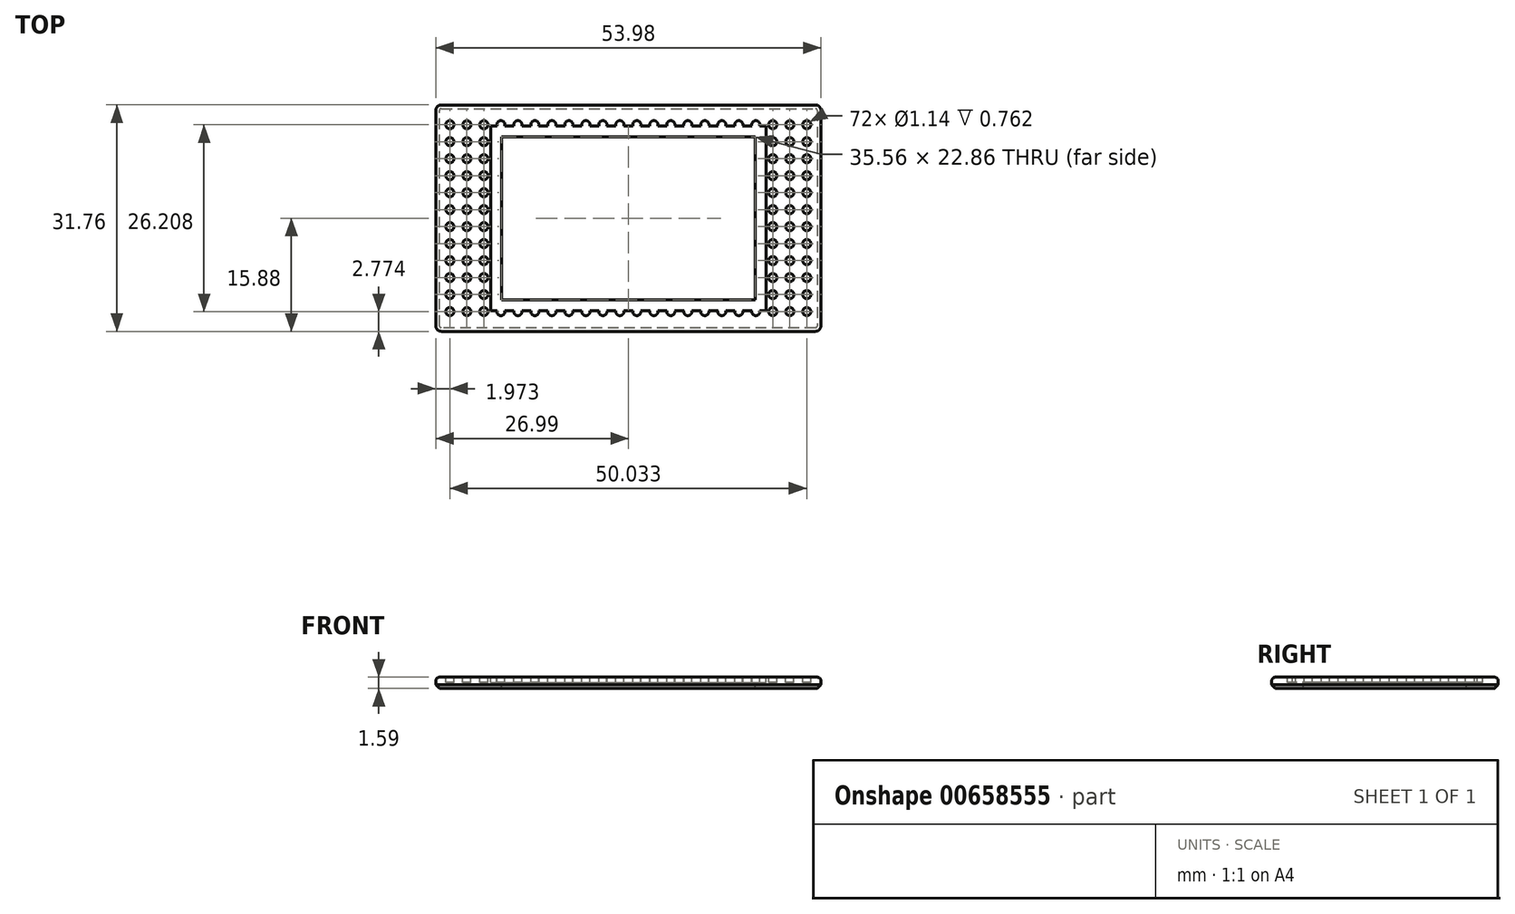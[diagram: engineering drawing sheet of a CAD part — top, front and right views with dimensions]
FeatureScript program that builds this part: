
annotation { "Feature Type Name" : "Feature", "Feature Type Description" : "" }
export const myFeature = defineFeature(function(context is Context, id is Id, definition is map)
    precondition{}
    {
        {
            var Q0;
            Q0=qCreatedBy(makeId("Top.planeOp"),FACE);
            var sketch = newSketch(context, id + "F0", { "sketchPlane" : qUnion([Q0])});
            skLineSegment(sketch, "E0.bottom", {"start": v(-26.99, 15.88) * mm, "end": v(26.99, 15.88) * mm});
            skLineSegment(sketch, "E0.top", {"start": v(-26.99, -15.88) * mm, "end": v(26.99, -15.88) * mm});
            skLineSegment(sketch, "E0.left", {"start": v(-26.99, 15.87) * mm, "end": v(-26.99, -15.88) * mm});
            skLineSegment(sketch, "E0.right", {"start": v(26.99, 15.88) * mm, "end": v(26.99, -15.87) * mm});
            skSolve(sketch);
        }
        {
            var Q0;
            Q0 = qSketchRegion(id + "F0", true);
            extrude(context, id + "F1", {"entities" : qUnion([Q0]), "depth" : 1.59 * mm, "offsetDistance" : 25.4 * mm});
        }
        {
            var Q0;
            Q0=makeQuery(id+"F1.opExtrude","CAP_FACE",FACE,{"disambiguationData":[OSD([sQuery(id+"F0.wireOp",EDGE,"E0.bottom"),sQuery(id+"F0.wireOp",EDGE,"E0.top"),sQuery(id+"F0.wireOp",EDGE,"E0.left"),sQuery(id+"F0.wireOp",EDGE,"E0.right")])],"isStart":false});
            var sketch = newSketch(context, id + "F2", { "sketchPlane" : qUnion([Q0])});
            skCircle(sketch, "E1", {"center": v(-25.02, -13.1) * mm, "radius": 0.57 * mm});
            skCircle(sketch, "E2.0.1.0", {"center": v(-25.02, -10.72) * mm, "radius": 0.57 * mm});
            skCircle(sketch, "E2.0.2.0", {"center": v(-25.02, -8.34) * mm, "radius": 0.57 * mm});
            skCircle(sketch, "E2.0.3.0", {"center": v(-25.02, -5.96) * mm, "radius": 0.57 * mm});
            skCircle(sketch, "E2.0.4.0", {"center": v(-25.02, -3.58) * mm, "radius": 0.57 * mm});
            skCircle(sketch, "E2.0.5.0", {"center": v(-25.02, -1.2) * mm, "radius": 0.57 * mm});
            skCircle(sketch, "E2.0.6.0", {"center": v(-25.02, 1.19) * mm, "radius": 0.57 * mm});
            skCircle(sketch, "E2.0.7.0", {"center": v(-25.02, 3.57) * mm, "radius": 0.57 * mm});
            skCircle(sketch, "E2.0.8.0", {"center": v(-25.02, 5.95) * mm, "radius": 0.57 * mm});
            skCircle(sketch, "E2.0.9.0", {"center": v(-25.02, 8.34) * mm, "radius": 0.57 * mm});
            skCircle(sketch, "E2.0.10.0", {"center": v(-25.02, 10.72) * mm, "radius": 0.57 * mm});
            skCircle(sketch, "E2.0.11.0", {"center": v(-25.02, 13.1) * mm, "radius": 0.57 * mm});
            skCircle(sketch, "E2.1.0.0", {"center": v(-22.63, -13.1) * mm, "radius": 0.57 * mm});
            skCircle(sketch, "E2.1.1.0", {"center": v(-22.63, -10.72) * mm, "radius": 0.57 * mm});
            skCircle(sketch, "E2.1.2.0", {"center": v(-22.63, -8.34) * mm, "radius": 0.57 * mm});
            skCircle(sketch, "E2.1.3.0", {"center": v(-22.63, -5.96) * mm, "radius": 0.57 * mm});
            skCircle(sketch, "E2.1.4.0", {"center": v(-22.63, -3.58) * mm, "radius": 0.57 * mm});
            skCircle(sketch, "E2.1.5.0", {"center": v(-22.63, -1.2) * mm, "radius": 0.57 * mm});
            skCircle(sketch, "E2.1.6.0", {"center": v(-22.63, 1.19) * mm, "radius": 0.57 * mm});
            skCircle(sketch, "E2.1.7.0", {"center": v(-22.63, 3.57) * mm, "radius": 0.57 * mm});
            skCircle(sketch, "E2.1.8.0", {"center": v(-22.63, 5.95) * mm, "radius": 0.57 * mm});
            skCircle(sketch, "E2.1.9.0", {"center": v(-22.63, 8.34) * mm, "radius": 0.57 * mm});
            skCircle(sketch, "E2.1.10.0", {"center": v(-22.63, 10.72) * mm, "radius": 0.57 * mm});
            skCircle(sketch, "E2.1.11.0", {"center": v(-22.63, 13.1) * mm, "radius": 0.57 * mm});
            skCircle(sketch, "E2.2.0.0", {"center": v(-20.25, -13.1) * mm, "radius": 0.57 * mm});
            skCircle(sketch, "E2.2.1.0", {"center": v(-20.25, -10.72) * mm, "radius": 0.57 * mm});
            skCircle(sketch, "E2.2.2.0", {"center": v(-20.25, -8.34) * mm, "radius": 0.57 * mm});
            skCircle(sketch, "E2.2.3.0", {"center": v(-20.25, -5.96) * mm, "radius": 0.57 * mm});
            skCircle(sketch, "E2.2.4.0", {"center": v(-20.25, -3.58) * mm, "radius": 0.57 * mm});
            skCircle(sketch, "E2.2.5.0", {"center": v(-20.25, -1.2) * mm, "radius": 0.57 * mm});
            skCircle(sketch, "E2.2.6.0", {"center": v(-20.25, 1.19) * mm, "radius": 0.57 * mm});
            skCircle(sketch, "E2.2.7.0", {"center": v(-20.25, 3.57) * mm, "radius": 0.57 * mm});
            skCircle(sketch, "E2.2.8.0", {"center": v(-20.25, 5.95) * mm, "radius": 0.57 * mm});
            skCircle(sketch, "E2.2.9.0", {"center": v(-20.25, 8.34) * mm, "radius": 0.57 * mm});
            skCircle(sketch, "E2.2.10.0", {"center": v(-20.25, 10.72) * mm, "radius": 0.57 * mm});
            skCircle(sketch, "E2.2.11.0", {"center": v(-20.25, 13.1) * mm, "radius": 0.57 * mm});
            skCircle(sketch, "E2.3.0.0", {"center": v(-17.87, -13.1) * mm, "radius": 0.57 * mm});
            skCircle(sketch, "E2.3.1.0", {"center": v(-17.87, -10.72) * mm, "radius": 0.57 * mm});
            skCircle(sketch, "E2.3.2.0", {"center": v(-17.87, -8.34) * mm, "radius": 0.57 * mm});
            skCircle(sketch, "E2.3.3.0", {"center": v(-17.87, -5.96) * mm, "radius": 0.57 * mm});
            skCircle(sketch, "E2.3.4.0", {"center": v(-17.87, -3.58) * mm, "radius": 0.57 * mm});
            skCircle(sketch, "E2.3.5.0", {"center": v(-17.87, -1.2) * mm, "radius": 0.57 * mm});
            skCircle(sketch, "E2.3.6.0", {"center": v(-17.87, 1.19) * mm, "radius": 0.57 * mm});
            skCircle(sketch, "E2.3.7.0", {"center": v(-17.87, 3.57) * mm, "radius": 0.57 * mm});
            skCircle(sketch, "E2.3.8.0", {"center": v(-17.87, 5.95) * mm, "radius": 0.57 * mm});
            skCircle(sketch, "E2.3.9.0", {"center": v(-17.87, 8.34) * mm, "radius": 0.57 * mm});
            skCircle(sketch, "E2.3.10.0", {"center": v(-17.87, 10.72) * mm, "radius": 0.57 * mm});
            skCircle(sketch, "E2.3.11.0", {"center": v(-17.87, 13.1) * mm, "radius": 0.57 * mm});
            skCircle(sketch, "E2.4.0.0", {"center": v(-15.49, -13.1) * mm, "radius": 0.57 * mm});
            skCircle(sketch, "E2.4.1.0", {"center": v(-15.49, -10.72) * mm, "radius": 0.57 * mm});
            skCircle(sketch, "E2.4.2.0", {"center": v(-15.49, -8.34) * mm, "radius": 0.57 * mm});
            skCircle(sketch, "E2.4.3.0", {"center": v(-15.49, -5.96) * mm, "radius": 0.57 * mm});
            skCircle(sketch, "E2.4.4.0", {"center": v(-15.49, -3.58) * mm, "radius": 0.57 * mm});
            skCircle(sketch, "E2.4.5.0", {"center": v(-15.49, -1.2) * mm, "radius": 0.57 * mm});
            skCircle(sketch, "E2.4.6.0", {"center": v(-15.49, 1.19) * mm, "radius": 0.57 * mm});
            skCircle(sketch, "E2.4.7.0", {"center": v(-15.49, 3.57) * mm, "radius": 0.57 * mm});
            skCircle(sketch, "E2.4.8.0", {"center": v(-15.49, 5.95) * mm, "radius": 0.57 * mm});
            skCircle(sketch, "E2.4.9.0", {"center": v(-15.49, 8.34) * mm, "radius": 0.57 * mm});
            skCircle(sketch, "E2.4.10.0", {"center": v(-15.49, 10.72) * mm, "radius": 0.57 * mm});
            skCircle(sketch, "E2.4.11.0", {"center": v(-15.49, 13.1) * mm, "radius": 0.57 * mm});
            skCircle(sketch, "E2.5.0.0", {"center": v(-13.1, -13.1) * mm, "radius": 0.57 * mm});
            skCircle(sketch, "E2.5.1.0", {"center": v(-13.1, -10.72) * mm, "radius": 0.57 * mm});
            skCircle(sketch, "E2.5.2.0", {"center": v(-13.1, -8.34) * mm, "radius": 0.57 * mm});
            skCircle(sketch, "E2.5.3.0", {"center": v(-13.1, -5.96) * mm, "radius": 0.57 * mm});
            skCircle(sketch, "E2.5.4.0", {"center": v(-13.1, -3.58) * mm, "radius": 0.57 * mm});
            skCircle(sketch, "E2.5.5.0", {"center": v(-13.1, -1.2) * mm, "radius": 0.57 * mm});
            skCircle(sketch, "E2.5.6.0", {"center": v(-13.1, 1.19) * mm, "radius": 0.57 * mm});
            skCircle(sketch, "E2.5.7.0", {"center": v(-13.1, 3.57) * mm, "radius": 0.57 * mm});
            skCircle(sketch, "E2.5.8.0", {"center": v(-13.1, 5.95) * mm, "radius": 0.57 * mm});
            skCircle(sketch, "E2.5.9.0", {"center": v(-13.1, 8.34) * mm, "radius": 0.57 * mm});
            skCircle(sketch, "E2.5.10.0", {"center": v(-13.1, 10.72) * mm, "radius": 0.57 * mm});
            skCircle(sketch, "E2.5.11.0", {"center": v(-13.1, 13.1) * mm, "radius": 0.57 * mm});
            skCircle(sketch, "E2.6.0.0", {"center": v(-10.72, -13.1) * mm, "radius": 0.57 * mm});
            skCircle(sketch, "E2.6.1.0", {"center": v(-10.72, -10.72) * mm, "radius": 0.57 * mm});
            skCircle(sketch, "E2.6.2.0", {"center": v(-10.72, -8.34) * mm, "radius": 0.57 * mm});
            skCircle(sketch, "E2.6.3.0", {"center": v(-10.72, -5.96) * mm, "radius": 0.57 * mm});
            skCircle(sketch, "E2.6.4.0", {"center": v(-10.72, -3.58) * mm, "radius": 0.57 * mm});
            skCircle(sketch, "E2.6.5.0", {"center": v(-10.72, -1.2) * mm, "radius": 0.57 * mm});
            skCircle(sketch, "E2.6.6.0", {"center": v(-10.72, 1.19) * mm, "radius": 0.57 * mm});
            skCircle(sketch, "E2.6.7.0", {"center": v(-10.72, 3.57) * mm, "radius": 0.57 * mm});
            skCircle(sketch, "E2.6.8.0", {"center": v(-10.72, 5.95) * mm, "radius": 0.57 * mm});
            skCircle(sketch, "E2.6.9.0", {"center": v(-10.72, 8.34) * mm, "radius": 0.57 * mm});
            skCircle(sketch, "E2.6.10.0", {"center": v(-10.72, 10.72) * mm, "radius": 0.57 * mm});
            skCircle(sketch, "E2.6.11.0", {"center": v(-10.72, 13.1) * mm, "radius": 0.57 * mm});
            skCircle(sketch, "E2.7.0.0", {"center": v(-8.34, -13.1) * mm, "radius": 0.57 * mm});
            skCircle(sketch, "E2.7.1.0", {"center": v(-8.34, -10.72) * mm, "radius": 0.57 * mm});
            skCircle(sketch, "E2.7.2.0", {"center": v(-8.34, -8.34) * mm, "radius": 0.57 * mm});
            skCircle(sketch, "E2.7.3.0", {"center": v(-8.34, -5.96) * mm, "radius": 0.57 * mm});
            skCircle(sketch, "E2.7.4.0", {"center": v(-8.34, -3.58) * mm, "radius": 0.57 * mm});
            skCircle(sketch, "E2.7.5.0", {"center": v(-8.34, -1.2) * mm, "radius": 0.57 * mm});
            skCircle(sketch, "E2.7.6.0", {"center": v(-8.34, 1.19) * mm, "radius": 0.57 * mm});
            skCircle(sketch, "E2.7.7.0", {"center": v(-8.34, 3.57) * mm, "radius": 0.57 * mm});
            skCircle(sketch, "E2.7.8.0", {"center": v(-8.34, 5.95) * mm, "radius": 0.57 * mm});
            skCircle(sketch, "E2.7.9.0", {"center": v(-8.34, 8.34) * mm, "radius": 0.57 * mm});
            skCircle(sketch, "E2.7.10.0", {"center": v(-8.34, 10.72) * mm, "radius": 0.57 * mm});
            skCircle(sketch, "E2.7.11.0", {"center": v(-8.34, 13.1) * mm, "radius": 0.57 * mm});
            skCircle(sketch, "E2.8.0.0", {"center": v(-5.96, -13.1) * mm, "radius": 0.57 * mm});
            skCircle(sketch, "E2.8.1.0", {"center": v(-5.96, -10.72) * mm, "radius": 0.57 * mm});
            skCircle(sketch, "E2.8.2.0", {"center": v(-5.96, -8.34) * mm, "radius": 0.57 * mm});
            skCircle(sketch, "E2.8.3.0", {"center": v(-5.96, -5.96) * mm, "radius": 0.57 * mm});
            skCircle(sketch, "E2.8.4.0", {"center": v(-5.96, -3.58) * mm, "radius": 0.57 * mm});
            skCircle(sketch, "E2.8.5.0", {"center": v(-5.96, -1.2) * mm, "radius": 0.57 * mm});
            skCircle(sketch, "E2.8.6.0", {"center": v(-5.96, 1.19) * mm, "radius": 0.57 * mm});
            skCircle(sketch, "E2.8.7.0", {"center": v(-5.96, 3.57) * mm, "radius": 0.57 * mm});
            skCircle(sketch, "E2.8.8.0", {"center": v(-5.96, 5.95) * mm, "radius": 0.57 * mm});
            skCircle(sketch, "E2.8.9.0", {"center": v(-5.96, 8.34) * mm, "radius": 0.57 * mm});
            skCircle(sketch, "E2.8.10.0", {"center": v(-5.96, 10.72) * mm, "radius": 0.57 * mm});
            skCircle(sketch, "E2.8.11.0", {"center": v(-5.96, 13.1) * mm, "radius": 0.57 * mm});
            skCircle(sketch, "E2.9.0.0", {"center": v(-3.57, -13.1) * mm, "radius": 0.57 * mm});
            skCircle(sketch, "E2.9.1.0", {"center": v(-3.57, -10.72) * mm, "radius": 0.57 * mm});
            skCircle(sketch, "E2.9.2.0", {"center": v(-3.57, -8.34) * mm, "radius": 0.57 * mm});
            skCircle(sketch, "E2.9.3.0", {"center": v(-3.57, -5.96) * mm, "radius": 0.57 * mm});
            skCircle(sketch, "E2.9.4.0", {"center": v(-3.57, -3.58) * mm, "radius": 0.57 * mm});
            skCircle(sketch, "E2.9.5.0", {"center": v(-3.57, -1.2) * mm, "radius": 0.57 * mm});
            skCircle(sketch, "E2.9.6.0", {"center": v(-3.57, 1.19) * mm, "radius": 0.57 * mm});
            skCircle(sketch, "E2.9.7.0", {"center": v(-3.57, 3.57) * mm, "radius": 0.57 * mm});
            skCircle(sketch, "E2.9.8.0", {"center": v(-3.57, 5.95) * mm, "radius": 0.57 * mm});
            skCircle(sketch, "E2.9.9.0", {"center": v(-3.57, 8.34) * mm, "radius": 0.57 * mm});
            skCircle(sketch, "E2.9.10.0", {"center": v(-3.57, 10.72) * mm, "radius": 0.57 * mm});
            skCircle(sketch, "E2.9.11.0", {"center": v(-3.57, 13.1) * mm, "radius": 0.57 * mm});
            skCircle(sketch, "E2.10.0.0", {"center": v(-1.2, -13.1) * mm, "radius": 0.57 * mm});
            skCircle(sketch, "E2.10.1.0", {"center": v(-1.2, -10.72) * mm, "radius": 0.57 * mm});
            skCircle(sketch, "E2.10.2.0", {"center": v(-1.2, -8.34) * mm, "radius": 0.57 * mm});
            skCircle(sketch, "E2.10.3.0", {"center": v(-1.2, -5.96) * mm, "radius": 0.57 * mm});
            skCircle(sketch, "E2.10.4.0", {"center": v(-1.2, -3.58) * mm, "radius": 0.57 * mm});
            skCircle(sketch, "E2.10.5.0", {"center": v(-1.2, -1.2) * mm, "radius": 0.57 * mm});
            skCircle(sketch, "E2.10.6.0", {"center": v(-1.2, 1.19) * mm, "radius": 0.57 * mm});
            skCircle(sketch, "E2.10.7.0", {"center": v(-1.2, 3.57) * mm, "radius": 0.57 * mm});
            skCircle(sketch, "E2.10.8.0", {"center": v(-1.2, 5.95) * mm, "radius": 0.57 * mm});
            skCircle(sketch, "E2.10.9.0", {"center": v(-1.2, 8.34) * mm, "radius": 0.57 * mm});
            skCircle(sketch, "E2.10.10.0", {"center": v(-1.2, 10.72) * mm, "radius": 0.57 * mm});
            skCircle(sketch, "E2.10.11.0", {"center": v(-1.2, 13.1) * mm, "radius": 0.57 * mm});
            skCircle(sketch, "E2.11.0.0", {"center": v(1.2, -13.1) * mm, "radius": 0.57 * mm});
            skCircle(sketch, "E2.11.1.0", {"center": v(1.2, -10.72) * mm, "radius": 0.57 * mm});
            skCircle(sketch, "E2.11.2.0", {"center": v(1.2, -8.34) * mm, "radius": 0.57 * mm});
            skCircle(sketch, "E2.11.3.0", {"center": v(1.2, -5.96) * mm, "radius": 0.57 * mm});
            skCircle(sketch, "E2.11.4.0", {"center": v(1.2, -3.58) * mm, "radius": 0.57 * mm});
            skCircle(sketch, "E2.11.5.0", {"center": v(1.2, -1.2) * mm, "radius": 0.57 * mm});
            skCircle(sketch, "E2.11.6.0", {"center": v(1.2, 1.19) * mm, "radius": 0.57 * mm});
            skCircle(sketch, "E2.11.7.0", {"center": v(1.2, 3.57) * mm, "radius": 0.57 * mm});
            skCircle(sketch, "E2.11.8.0", {"center": v(1.2, 5.95) * mm, "radius": 0.57 * mm});
            skCircle(sketch, "E2.11.9.0", {"center": v(1.2, 8.34) * mm, "radius": 0.57 * mm});
            skCircle(sketch, "E2.11.10.0", {"center": v(1.2, 10.72) * mm, "radius": 0.57 * mm});
            skCircle(sketch, "E2.11.11.0", {"center": v(1.2, 13.1) * mm, "radius": 0.57 * mm});
            skCircle(sketch, "E2.12.0.0", {"center": v(3.57, -13.1) * mm, "radius": 0.57 * mm});
            skCircle(sketch, "E2.12.1.0", {"center": v(3.57, -10.72) * mm, "radius": 0.57 * mm});
            skCircle(sketch, "E2.12.2.0", {"center": v(3.57, -8.34) * mm, "radius": 0.57 * mm});
            skCircle(sketch, "E2.12.3.0", {"center": v(3.57, -5.96) * mm, "radius": 0.57 * mm});
            skCircle(sketch, "E2.12.4.0", {"center": v(3.57, -3.58) * mm, "radius": 0.57 * mm});
            skCircle(sketch, "E2.12.5.0", {"center": v(3.57, -1.2) * mm, "radius": 0.57 * mm});
            skCircle(sketch, "E2.12.6.0", {"center": v(3.57, 1.19) * mm, "radius": 0.57 * mm});
            skCircle(sketch, "E2.12.7.0", {"center": v(3.57, 3.57) * mm, "radius": 0.57 * mm});
            skCircle(sketch, "E2.12.8.0", {"center": v(3.57, 5.95) * mm, "radius": 0.57 * mm});
            skCircle(sketch, "E2.12.9.0", {"center": v(3.57, 8.34) * mm, "radius": 0.57 * mm});
            skCircle(sketch, "E2.12.10.0", {"center": v(3.57, 10.72) * mm, "radius": 0.57 * mm});
            skCircle(sketch, "E2.12.11.0", {"center": v(3.57, 13.1) * mm, "radius": 0.57 * mm});
            skCircle(sketch, "E2.13.0.0", {"center": v(5.96, -13.1) * mm, "radius": 0.57 * mm});
            skCircle(sketch, "E2.13.1.0", {"center": v(5.96, -10.72) * mm, "radius": 0.57 * mm});
            skCircle(sketch, "E2.13.2.0", {"center": v(5.96, -8.34) * mm, "radius": 0.57 * mm});
            skCircle(sketch, "E2.13.3.0", {"center": v(5.96, -5.96) * mm, "radius": 0.57 * mm});
            skCircle(sketch, "E2.13.4.0", {"center": v(5.96, -3.58) * mm, "radius": 0.57 * mm});
            skCircle(sketch, "E2.13.5.0", {"center": v(5.96, -1.2) * mm, "radius": 0.57 * mm});
            skCircle(sketch, "E2.13.6.0", {"center": v(5.96, 1.19) * mm, "radius": 0.57 * mm});
            skCircle(sketch, "E2.13.7.0", {"center": v(5.96, 3.57) * mm, "radius": 0.57 * mm});
            skCircle(sketch, "E2.13.8.0", {"center": v(5.96, 5.95) * mm, "radius": 0.57 * mm});
            skCircle(sketch, "E2.13.9.0", {"center": v(5.96, 8.34) * mm, "radius": 0.57 * mm});
            skCircle(sketch, "E2.13.10.0", {"center": v(5.96, 10.72) * mm, "radius": 0.57 * mm});
            skCircle(sketch, "E2.13.11.0", {"center": v(5.96, 13.1) * mm, "radius": 0.57 * mm});
            skCircle(sketch, "E2.14.0.0", {"center": v(8.34, -13.1) * mm, "radius": 0.57 * mm});
            skCircle(sketch, "E2.14.1.0", {"center": v(8.34, -10.72) * mm, "radius": 0.57 * mm});
            skCircle(sketch, "E2.14.2.0", {"center": v(8.34, -8.34) * mm, "radius": 0.57 * mm});
            skCircle(sketch, "E2.14.3.0", {"center": v(8.34, -5.96) * mm, "radius": 0.57 * mm});
            skCircle(sketch, "E2.14.4.0", {"center": v(8.34, -3.58) * mm, "radius": 0.57 * mm});
            skCircle(sketch, "E2.14.5.0", {"center": v(8.34, -1.2) * mm, "radius": 0.57 * mm});
            skCircle(sketch, "E2.14.6.0", {"center": v(8.34, 1.19) * mm, "radius": 0.57 * mm});
            skCircle(sketch, "E2.14.7.0", {"center": v(8.34, 3.57) * mm, "radius": 0.57 * mm});
            skCircle(sketch, "E2.14.8.0", {"center": v(8.34, 5.95) * mm, "radius": 0.57 * mm});
            skCircle(sketch, "E2.14.9.0", {"center": v(8.34, 8.34) * mm, "radius": 0.57 * mm});
            skCircle(sketch, "E2.14.10.0", {"center": v(8.34, 10.72) * mm, "radius": 0.57 * mm});
            skCircle(sketch, "E2.14.11.0", {"center": v(8.34, 13.1) * mm, "radius": 0.57 * mm});
            skCircle(sketch, "E2.15.0.0", {"center": v(10.72, -13.1) * mm, "radius": 0.57 * mm});
            skCircle(sketch, "E2.15.1.0", {"center": v(10.72, -10.72) * mm, "radius": 0.57 * mm});
            skCircle(sketch, "E2.15.2.0", {"center": v(10.72, -8.34) * mm, "radius": 0.57 * mm});
            skCircle(sketch, "E2.15.3.0", {"center": v(10.72, -5.96) * mm, "radius": 0.57 * mm});
            skCircle(sketch, "E2.15.4.0", {"center": v(10.72, -3.58) * mm, "radius": 0.57 * mm});
            skCircle(sketch, "E2.15.5.0", {"center": v(10.72, -1.2) * mm, "radius": 0.57 * mm});
            skCircle(sketch, "E2.15.6.0", {"center": v(10.72, 1.19) * mm, "radius": 0.57 * mm});
            skCircle(sketch, "E2.15.7.0", {"center": v(10.72, 3.57) * mm, "radius": 0.57 * mm});
            skCircle(sketch, "E2.15.8.0", {"center": v(10.72, 5.95) * mm, "radius": 0.57 * mm});
            skCircle(sketch, "E2.15.9.0", {"center": v(10.72, 8.34) * mm, "radius": 0.57 * mm});
            skCircle(sketch, "E2.15.10.0", {"center": v(10.72, 10.72) * mm, "radius": 0.57 * mm});
            skCircle(sketch, "E2.15.11.0", {"center": v(10.72, 13.1) * mm, "radius": 0.57 * mm});
            skCircle(sketch, "E2.16.0.0", {"center": v(13.1, -13.1) * mm, "radius": 0.57 * mm});
            skCircle(sketch, "E2.16.1.0", {"center": v(13.1, -10.72) * mm, "radius": 0.57 * mm});
            skCircle(sketch, "E2.16.2.0", {"center": v(13.1, -8.34) * mm, "radius": 0.57 * mm});
            skCircle(sketch, "E2.16.3.0", {"center": v(13.1, -5.96) * mm, "radius": 0.57 * mm});
            skCircle(sketch, "E2.16.4.0", {"center": v(13.1, -3.58) * mm, "radius": 0.57 * mm});
            skCircle(sketch, "E2.16.5.0", {"center": v(13.1, -1.2) * mm, "radius": 0.57 * mm});
            skCircle(sketch, "E2.16.6.0", {"center": v(13.1, 1.19) * mm, "radius": 0.57 * mm});
            skCircle(sketch, "E2.16.7.0", {"center": v(13.1, 3.57) * mm, "radius": 0.57 * mm});
            skCircle(sketch, "E2.16.8.0", {"center": v(13.1, 5.95) * mm, "radius": 0.57 * mm});
            skCircle(sketch, "E2.16.9.0", {"center": v(13.1, 8.34) * mm, "radius": 0.57 * mm});
            skCircle(sketch, "E2.16.10.0", {"center": v(13.1, 10.72) * mm, "radius": 0.57 * mm});
            skCircle(sketch, "E2.16.11.0", {"center": v(13.1, 13.1) * mm, "radius": 0.57 * mm});
            skCircle(sketch, "E2.17.0.0", {"center": v(15.49, -13.1) * mm, "radius": 0.57 * mm});
            skCircle(sketch, "E2.17.1.0", {"center": v(15.49, -10.72) * mm, "radius": 0.57 * mm});
            skCircle(sketch, "E2.17.2.0", {"center": v(15.49, -8.34) * mm, "radius": 0.57 * mm});
            skCircle(sketch, "E2.17.3.0", {"center": v(15.49, -5.96) * mm, "radius": 0.57 * mm});
            skCircle(sketch, "E2.17.4.0", {"center": v(15.49, -3.58) * mm, "radius": 0.57 * mm});
            skCircle(sketch, "E2.17.5.0", {"center": v(15.49, -1.2) * mm, "radius": 0.57 * mm});
            skCircle(sketch, "E2.17.6.0", {"center": v(15.49, 1.19) * mm, "radius": 0.57 * mm});
            skCircle(sketch, "E2.17.7.0", {"center": v(15.49, 3.57) * mm, "radius": 0.57 * mm});
            skCircle(sketch, "E2.17.8.0", {"center": v(15.49, 5.95) * mm, "radius": 0.57 * mm});
            skCircle(sketch, "E2.17.9.0", {"center": v(15.49, 8.34) * mm, "radius": 0.57 * mm});
            skCircle(sketch, "E2.17.10.0", {"center": v(15.49, 10.72) * mm, "radius": 0.57 * mm});
            skCircle(sketch, "E2.17.11.0", {"center": v(15.49, 13.1) * mm, "radius": 0.57 * mm});
            skCircle(sketch, "E2.18.0.0", {"center": v(17.87, -13.1) * mm, "radius": 0.57 * mm});
            skCircle(sketch, "E2.18.1.0", {"center": v(17.87, -10.72) * mm, "radius": 0.57 * mm});
            skCircle(sketch, "E2.18.2.0", {"center": v(17.87, -8.34) * mm, "radius": 0.57 * mm});
            skCircle(sketch, "E2.18.3.0", {"center": v(17.87, -5.96) * mm, "radius": 0.57 * mm});
            skCircle(sketch, "E2.18.4.0", {"center": v(17.87, -3.58) * mm, "radius": 0.57 * mm});
            skCircle(sketch, "E2.18.5.0", {"center": v(17.87, -1.2) * mm, "radius": 0.57 * mm});
            skCircle(sketch, "E2.18.6.0", {"center": v(17.87, 1.19) * mm, "radius": 0.57 * mm});
            skCircle(sketch, "E2.18.7.0", {"center": v(17.87, 3.57) * mm, "radius": 0.57 * mm});
            skCircle(sketch, "E2.18.8.0", {"center": v(17.87, 5.95) * mm, "radius": 0.57 * mm});
            skCircle(sketch, "E2.18.9.0", {"center": v(17.87, 8.34) * mm, "radius": 0.57 * mm});
            skCircle(sketch, "E2.18.10.0", {"center": v(17.87, 10.72) * mm, "radius": 0.57 * mm});
            skCircle(sketch, "E2.18.11.0", {"center": v(17.87, 13.1) * mm, "radius": 0.57 * mm});
            skCircle(sketch, "E2.19.0.0", {"center": v(20.25, -13.1) * mm, "radius": 0.57 * mm});
            skCircle(sketch, "E2.19.1.0", {"center": v(20.25, -10.72) * mm, "radius": 0.57 * mm});
            skCircle(sketch, "E2.19.2.0", {"center": v(20.25, -8.34) * mm, "radius": 0.57 * mm});
            skCircle(sketch, "E2.19.3.0", {"center": v(20.25, -5.96) * mm, "radius": 0.57 * mm});
            skCircle(sketch, "E2.19.4.0", {"center": v(20.25, -3.58) * mm, "radius": 0.57 * mm});
            skCircle(sketch, "E2.19.5.0", {"center": v(20.25, -1.2) * mm, "radius": 0.57 * mm});
            skCircle(sketch, "E2.19.6.0", {"center": v(20.25, 1.19) * mm, "radius": 0.57 * mm});
            skCircle(sketch, "E2.19.7.0", {"center": v(20.25, 3.57) * mm, "radius": 0.57 * mm});
            skCircle(sketch, "E2.19.8.0", {"center": v(20.25, 5.95) * mm, "radius": 0.57 * mm});
            skCircle(sketch, "E2.19.9.0", {"center": v(20.25, 8.34) * mm, "radius": 0.57 * mm});
            skCircle(sketch, "E2.19.10.0", {"center": v(20.25, 10.72) * mm, "radius": 0.57 * mm});
            skCircle(sketch, "E2.19.11.0", {"center": v(20.25, 13.1) * mm, "radius": 0.57 * mm});
            skCircle(sketch, "E2.20.0.0", {"center": v(22.63, -13.1) * mm, "radius": 0.57 * mm});
            skCircle(sketch, "E2.20.1.0", {"center": v(22.63, -10.72) * mm, "radius": 0.57 * mm});
            skCircle(sketch, "E2.20.2.0", {"center": v(22.63, -8.34) * mm, "radius": 0.57 * mm});
            skCircle(sketch, "E2.20.3.0", {"center": v(22.63, -5.96) * mm, "radius": 0.57 * mm});
            skCircle(sketch, "E2.20.4.0", {"center": v(22.63, -3.58) * mm, "radius": 0.57 * mm});
            skCircle(sketch, "E2.20.5.0", {"center": v(22.63, -1.2) * mm, "radius": 0.57 * mm});
            skCircle(sketch, "E2.20.6.0", {"center": v(22.63, 1.19) * mm, "radius": 0.57 * mm});
            skCircle(sketch, "E2.20.7.0", {"center": v(22.63, 3.57) * mm, "radius": 0.57 * mm});
            skCircle(sketch, "E2.20.8.0", {"center": v(22.63, 5.95) * mm, "radius": 0.57 * mm});
            skCircle(sketch, "E2.20.9.0", {"center": v(22.63, 8.34) * mm, "radius": 0.57 * mm});
            skCircle(sketch, "E2.20.10.0", {"center": v(22.63, 10.72) * mm, "radius": 0.57 * mm});
            skCircle(sketch, "E2.20.11.0", {"center": v(22.63, 13.1) * mm, "radius": 0.57 * mm});
            skCircle(sketch, "E2.21.0.0", {"center": v(25.02, -13.1) * mm, "radius": 0.57 * mm});
            skCircle(sketch, "E2.21.1.0", {"center": v(25.02, -10.72) * mm, "radius": 0.57 * mm});
            skCircle(sketch, "E2.21.2.0", {"center": v(25.02, -8.34) * mm, "radius": 0.57 * mm});
            skCircle(sketch, "E2.21.3.0", {"center": v(25.02, -5.96) * mm, "radius": 0.57 * mm});
            skCircle(sketch, "E2.21.4.0", {"center": v(25.02, -3.58) * mm, "radius": 0.57 * mm});
            skCircle(sketch, "E2.21.5.0", {"center": v(25.02, -1.2) * mm, "radius": 0.57 * mm});
            skCircle(sketch, "E2.21.6.0", {"center": v(25.02, 1.19) * mm, "radius": 0.57 * mm});
            skCircle(sketch, "E2.21.7.0", {"center": v(25.02, 3.57) * mm, "radius": 0.57 * mm});
            skCircle(sketch, "E2.21.8.0", {"center": v(25.02, 5.95) * mm, "radius": 0.57 * mm});
            skCircle(sketch, "E2.21.9.0", {"center": v(25.02, 8.34) * mm, "radius": 0.57 * mm});
            skCircle(sketch, "E2.21.10.0", {"center": v(25.02, 10.72) * mm, "radius": 0.57 * mm});
            skCircle(sketch, "E2.21.11.0", {"center": v(25.02, 13.1) * mm, "radius": 0.57 * mm});
            skLineSegment(sketch, "E2.direction1", {"start": v(-25.02, -13.1) * mm, "end": v(-22.63, -13.1) * mm, "construction": true});
            skLineSegment(sketch, "E2.direction2", {"start": v(-25.02, -13.1) * mm, "end": v(-25.02, -10.72) * mm, "construction": true});
            skSolve(sketch);
        }
        {
            var Q0;
            Q0 = qSketchRegion(id + "F2", true);
            extrude(context, id + "F3", {"entities" : qUnion([Q0]), "operationType" : NewBodyOperationType.REMOVE, "oppositeDirection" : true, "depth" : 0.76 * mm, "offsetDistance" : 25.4 * mm});
        }
        {
            var Q0;
            Q0=makeQuery(id+"F1.opExtrude","SWEPT_EDGE",EDGE,{"disambiguationData":[OSD([sQuery(id+"F0.wireOp",EDGE,"E0.top"),sQuery(id+"F0.wireOp",EDGE,"E0.left")])]});
            var Q1;
            Q1=makeQuery(id+"F1.opExtrude","SWEPT_EDGE",EDGE,{"disambiguationData":[OSD([sQuery(id+"F0.wireOp",EDGE,"E0.bottom"),sQuery(id+"F0.wireOp",EDGE,"E0.left")])]});
            var Q2;
            Q2=makeQuery(id+"F1.opExtrude","SWEPT_EDGE",EDGE,{"disambiguationData":[OSD([sQuery(id+"F0.wireOp",EDGE,"E0.bottom"),sQuery(id+"F0.wireOp",EDGE,"E0.right")])]});
            var Q3;
            Q3=makeQuery(id+"F1.opExtrude","SWEPT_EDGE",EDGE,{"disambiguationData":[OSD([sQuery(id+"F0.wireOp",EDGE,"E0.top"),sQuery(id+"F0.wireOp",EDGE,"E0.right")])]});
            fillet(context, id + "F4", {"entities" : qUnion([Q0, Q1, Q2, Q3]), "radius" : 0.76 * mm, "tangentPropagation" : true, "allowEdgeOverflow" : false});
        }
        {
            var Q0;
            Q0=makeQuery(id+"F1.opExtrude","CAP_EDGE",EDGE,{"disambiguationData":[OSD([sQuery(id+"F0.wireOp",EDGE,"E0.right")])],"isStart":false});
            fillet(context, id + "F5", {"entities" : qUnion([Q0]), "radius" : 0.5 * mm, "tangentPropagation" : true, "allowEdgeOverflow" : false});
        }
        {
            var Q0;
            Q0=makeQuery(id+"F1.opExtrude","CAP_EDGE",EDGE,{"disambiguationData":[OSD([sQuery(id+"F0.wireOp",EDGE,"E0.right")])],"isStart":true});
            chamfer(context, id + "F6", {"entities" : qUnion([Q0]), "width" : 0.5 * mm, "tangentPropagation" : true});
        }
        {
            var Q0;
            Q0=makeQuery(id+"F1.opExtrude","CAP_FACE",FACE,{"disambiguationData":[OSD([sQuery(id+"F0.wireOp",EDGE,"E0.bottom"),sQuery(id+"F0.wireOp",EDGE,"E0.top"),sQuery(id+"F0.wireOp",EDGE,"E0.left"),sQuery(id+"F0.wireOp",EDGE,"E0.right")])],"isStart":false});
            var sketch = newSketch(context, id + "F7", { "sketchPlane" : qUnion([Q0])});
            skLineSegment(sketch, "E3.bottom", {"start": v(-19.3, 12.95) * mm, "end": v(19.3, 12.95) * mm});
            skLineSegment(sketch, "E3.top", {"start": v(-19.3, -12.95) * mm, "end": v(19.3, -12.95) * mm});
            skLineSegment(sketch, "E3.left", {"start": v(-19.3, 12.95) * mm, "end": v(-19.3, -12.95) * mm});
            skLineSegment(sketch, "E3.right", {"start": v(19.3, 12.95) * mm, "end": v(19.3, -12.95) * mm});
            skSolve(sketch);
        }
        {
            var Q0;
            Q0 = qSketchRegion(id + "F7", true);
            extrude(context, id + "F8", {"entities" : qUnion([Q0]), "operationType" : NewBodyOperationType.REMOVE, "oppositeDirection" : true, "depth" : 0.76 * mm, "offsetDistance" : 25.4 * mm});
        }
        {
            var Q0;
            Q0=makeQuery(id+"F8.boolean.opBoolean","MERGE",FACE,{"derivedFrom":[makeQuery(id+"F3.boolean.opBoolean","COPY",FACE,{"derivedFrom":makeQuery(id+"F3.opExtrude","CAP_FACE",FACE,{"disambiguationData":[OSD([sQuery(id+"F2.wireOp",EDGE,"E2.3.0.0")])],"isStart":false})}),makeQuery(id+"F3.boolean.opBoolean","COPY",FACE,{"derivedFrom":makeQuery(id+"F3.opExtrude","CAP_FACE",FACE,{"disambiguationData":[OSD([sQuery(id+"F2.wireOp",EDGE,"E2.3.1.0")])],"isStart":false})}),makeQuery(id+"F3.boolean.opBoolean","COPY",FACE,{"derivedFrom":makeQuery(id+"F3.opExtrude","CAP_FACE",FACE,{"disambiguationData":[OSD([sQuery(id+"F2.wireOp",EDGE,"E2.3.2.0")])],"isStart":false})}),makeQuery(id+"F3.boolean.opBoolean","COPY",FACE,{"derivedFrom":makeQuery(id+"F3.opExtrude","CAP_FACE",FACE,{"disambiguationData":[OSD([sQuery(id+"F2.wireOp",EDGE,"E2.3.3.0")])],"isStart":false})}),makeQuery(id+"F3.boolean.opBoolean","COPY",FACE,{"derivedFrom":makeQuery(id+"F3.opExtrude","CAP_FACE",FACE,{"disambiguationData":[OSD([sQuery(id+"F2.wireOp",EDGE,"E2.3.4.0")])],"isStart":false})}),makeQuery(id+"F3.boolean.opBoolean","COPY",FACE,{"derivedFrom":makeQuery(id+"F3.opExtrude","CAP_FACE",FACE,{"disambiguationData":[OSD([sQuery(id+"F2.wireOp",EDGE,"E2.3.5.0")])],"isStart":false})}),makeQuery(id+"F3.boolean.opBoolean","COPY",FACE,{"derivedFrom":makeQuery(id+"F3.opExtrude","CAP_FACE",FACE,{"disambiguationData":[OSD([sQuery(id+"F2.wireOp",EDGE,"E2.3.6.0")])],"isStart":false})}),makeQuery(id+"F3.boolean.opBoolean","COPY",FACE,{"derivedFrom":makeQuery(id+"F3.opExtrude","CAP_FACE",FACE,{"disambiguationData":[OSD([sQuery(id+"F2.wireOp",EDGE,"E2.3.7.0")])],"isStart":false})}),makeQuery(id+"F3.boolean.opBoolean","COPY",FACE,{"derivedFrom":makeQuery(id+"F3.opExtrude","CAP_FACE",FACE,{"disambiguationData":[OSD([sQuery(id+"F2.wireOp",EDGE,"E2.3.8.0")])],"isStart":false})}),makeQuery(id+"F3.boolean.opBoolean","COPY",FACE,{"derivedFrom":makeQuery(id+"F3.opExtrude","CAP_FACE",FACE,{"disambiguationData":[OSD([sQuery(id+"F2.wireOp",EDGE,"E2.3.9.0")])],"isStart":false})}),makeQuery(id+"F3.boolean.opBoolean","COPY",FACE,{"derivedFrom":makeQuery(id+"F3.opExtrude","CAP_FACE",FACE,{"disambiguationData":[OSD([sQuery(id+"F2.wireOp",EDGE,"E2.3.10.0")])],"isStart":false})}),makeQuery(id+"F3.boolean.opBoolean","COPY",FACE,{"derivedFrom":makeQuery(id+"F3.opExtrude","CAP_FACE",FACE,{"disambiguationData":[OSD([sQuery(id+"F2.wireOp",EDGE,"E2.3.11.0")])],"isStart":false})}),makeQuery(id+"F3.boolean.opBoolean","COPY",FACE,{"derivedFrom":makeQuery(id+"F3.opExtrude","CAP_FACE",FACE,{"disambiguationData":[OSD([sQuery(id+"F2.wireOp",EDGE,"E2.4.0.0")])],"isStart":false})}),makeQuery(id+"F3.boolean.opBoolean","COPY",FACE,{"derivedFrom":makeQuery(id+"F3.opExtrude","CAP_FACE",FACE,{"disambiguationData":[OSD([sQuery(id+"F2.wireOp",EDGE,"E2.4.1.0")])],"isStart":false})}),makeQuery(id+"F3.boolean.opBoolean","COPY",FACE,{"derivedFrom":makeQuery(id+"F3.opExtrude","CAP_FACE",FACE,{"disambiguationData":[OSD([sQuery(id+"F2.wireOp",EDGE,"E2.4.2.0")])],"isStart":false})}),makeQuery(id+"F3.boolean.opBoolean","COPY",FACE,{"derivedFrom":makeQuery(id+"F3.opExtrude","CAP_FACE",FACE,{"disambiguationData":[OSD([sQuery(id+"F2.wireOp",EDGE,"E2.4.3.0")])],"isStart":false})}),makeQuery(id+"F3.boolean.opBoolean","COPY",FACE,{"derivedFrom":makeQuery(id+"F3.opExtrude","CAP_FACE",FACE,{"disambiguationData":[OSD([sQuery(id+"F2.wireOp",EDGE,"E2.4.4.0")])],"isStart":false})}),makeQuery(id+"F3.boolean.opBoolean","COPY",FACE,{"derivedFrom":makeQuery(id+"F3.opExtrude","CAP_FACE",FACE,{"disambiguationData":[OSD([sQuery(id+"F2.wireOp",EDGE,"E2.4.5.0")])],"isStart":false})}),makeQuery(id+"F3.boolean.opBoolean","COPY",FACE,{"derivedFrom":makeQuery(id+"F3.opExtrude","CAP_FACE",FACE,{"disambiguationData":[OSD([sQuery(id+"F2.wireOp",EDGE,"E2.4.6.0")])],"isStart":false})}),makeQuery(id+"F3.boolean.opBoolean","COPY",FACE,{"derivedFrom":makeQuery(id+"F3.opExtrude","CAP_FACE",FACE,{"disambiguationData":[OSD([sQuery(id+"F2.wireOp",EDGE,"E2.4.7.0")])],"isStart":false})}),makeQuery(id+"F3.boolean.opBoolean","COPY",FACE,{"derivedFrom":makeQuery(id+"F3.opExtrude","CAP_FACE",FACE,{"disambiguationData":[OSD([sQuery(id+"F2.wireOp",EDGE,"E2.4.8.0")])],"isStart":false})}),makeQuery(id+"F3.boolean.opBoolean","COPY",FACE,{"derivedFrom":makeQuery(id+"F3.opExtrude","CAP_FACE",FACE,{"disambiguationData":[OSD([sQuery(id+"F2.wireOp",EDGE,"E2.4.9.0")])],"isStart":false})}),makeQuery(id+"F3.boolean.opBoolean","COPY",FACE,{"derivedFrom":makeQuery(id+"F3.opExtrude","CAP_FACE",FACE,{"disambiguationData":[OSD([sQuery(id+"F2.wireOp",EDGE,"E2.4.10.0")])],"isStart":false})}),makeQuery(id+"F3.boolean.opBoolean","COPY",FACE,{"derivedFrom":makeQuery(id+"F3.opExtrude","CAP_FACE",FACE,{"disambiguationData":[OSD([sQuery(id+"F2.wireOp",EDGE,"E2.4.11.0")])],"isStart":false})}),makeQuery(id+"F3.boolean.opBoolean","COPY",FACE,{"derivedFrom":makeQuery(id+"F3.opExtrude","CAP_FACE",FACE,{"disambiguationData":[OSD([sQuery(id+"F2.wireOp",EDGE,"E2.5.0.0")])],"isStart":false})}),makeQuery(id+"F3.boolean.opBoolean","COPY",FACE,{"derivedFrom":makeQuery(id+"F3.opExtrude","CAP_FACE",FACE,{"disambiguationData":[OSD([sQuery(id+"F2.wireOp",EDGE,"E2.5.1.0")])],"isStart":false})}),makeQuery(id+"F3.boolean.opBoolean","COPY",FACE,{"derivedFrom":makeQuery(id+"F3.opExtrude","CAP_FACE",FACE,{"disambiguationData":[OSD([sQuery(id+"F2.wireOp",EDGE,"E2.5.2.0")])],"isStart":false})}),makeQuery(id+"F3.boolean.opBoolean","COPY",FACE,{"derivedFrom":makeQuery(id+"F3.opExtrude","CAP_FACE",FACE,{"disambiguationData":[OSD([sQuery(id+"F2.wireOp",EDGE,"E2.5.3.0")])],"isStart":false})}),makeQuery(id+"F3.boolean.opBoolean","COPY",FACE,{"derivedFrom":makeQuery(id+"F3.opExtrude","CAP_FACE",FACE,{"disambiguationData":[OSD([sQuery(id+"F2.wireOp",EDGE,"E2.5.4.0")])],"isStart":false})}),makeQuery(id+"F3.boolean.opBoolean","COPY",FACE,{"derivedFrom":makeQuery(id+"F3.opExtrude","CAP_FACE",FACE,{"disambiguationData":[OSD([sQuery(id+"F2.wireOp",EDGE,"E2.5.5.0")])],"isStart":false})}),makeQuery(id+"F3.boolean.opBoolean","COPY",FACE,{"derivedFrom":makeQuery(id+"F3.opExtrude","CAP_FACE",FACE,{"disambiguationData":[OSD([sQuery(id+"F2.wireOp",EDGE,"E2.5.6.0")])],"isStart":false})}),makeQuery(id+"F3.boolean.opBoolean","COPY",FACE,{"derivedFrom":makeQuery(id+"F3.opExtrude","CAP_FACE",FACE,{"disambiguationData":[OSD([sQuery(id+"F2.wireOp",EDGE,"E2.5.7.0")])],"isStart":false})}),makeQuery(id+"F3.boolean.opBoolean","COPY",FACE,{"derivedFrom":makeQuery(id+"F3.opExtrude","CAP_FACE",FACE,{"disambiguationData":[OSD([sQuery(id+"F2.wireOp",EDGE,"E2.5.8.0")])],"isStart":false})}),makeQuery(id+"F3.boolean.opBoolean","COPY",FACE,{"derivedFrom":makeQuery(id+"F3.opExtrude","CAP_FACE",FACE,{"disambiguationData":[OSD([sQuery(id+"F2.wireOp",EDGE,"E2.5.9.0")])],"isStart":false})}),makeQuery(id+"F3.boolean.opBoolean","COPY",FACE,{"derivedFrom":makeQuery(id+"F3.opExtrude","CAP_FACE",FACE,{"disambiguationData":[OSD([sQuery(id+"F2.wireOp",EDGE,"E2.5.10.0")])],"isStart":false})}),makeQuery(id+"F3.boolean.opBoolean","COPY",FACE,{"derivedFrom":makeQuery(id+"F3.opExtrude","CAP_FACE",FACE,{"disambiguationData":[OSD([sQuery(id+"F2.wireOp",EDGE,"E2.5.11.0")])],"isStart":false})}),makeQuery(id+"F3.boolean.opBoolean","COPY",FACE,{"derivedFrom":makeQuery(id+"F3.opExtrude","CAP_FACE",FACE,{"disambiguationData":[OSD([sQuery(id+"F2.wireOp",EDGE,"E2.6.0.0")])],"isStart":false})}),makeQuery(id+"F3.boolean.opBoolean","COPY",FACE,{"derivedFrom":makeQuery(id+"F3.opExtrude","CAP_FACE",FACE,{"disambiguationData":[OSD([sQuery(id+"F2.wireOp",EDGE,"E2.6.1.0")])],"isStart":false})}),makeQuery(id+"F3.boolean.opBoolean","COPY",FACE,{"derivedFrom":makeQuery(id+"F3.opExtrude","CAP_FACE",FACE,{"disambiguationData":[OSD([sQuery(id+"F2.wireOp",EDGE,"E2.6.2.0")])],"isStart":false})}),makeQuery(id+"F3.boolean.opBoolean","COPY",FACE,{"derivedFrom":makeQuery(id+"F3.opExtrude","CAP_FACE",FACE,{"disambiguationData":[OSD([sQuery(id+"F2.wireOp",EDGE,"E2.6.3.0")])],"isStart":false})}),makeQuery(id+"F3.boolean.opBoolean","COPY",FACE,{"derivedFrom":makeQuery(id+"F3.opExtrude","CAP_FACE",FACE,{"disambiguationData":[OSD([sQuery(id+"F2.wireOp",EDGE,"E2.6.4.0")])],"isStart":false})}),makeQuery(id+"F3.boolean.opBoolean","COPY",FACE,{"derivedFrom":makeQuery(id+"F3.opExtrude","CAP_FACE",FACE,{"disambiguationData":[OSD([sQuery(id+"F2.wireOp",EDGE,"E2.6.5.0")])],"isStart":false})}),makeQuery(id+"F3.boolean.opBoolean","COPY",FACE,{"derivedFrom":makeQuery(id+"F3.opExtrude","CAP_FACE",FACE,{"disambiguationData":[OSD([sQuery(id+"F2.wireOp",EDGE,"E2.6.6.0")])],"isStart":false})}),makeQuery(id+"F3.boolean.opBoolean","COPY",FACE,{"derivedFrom":makeQuery(id+"F3.opExtrude","CAP_FACE",FACE,{"disambiguationData":[OSD([sQuery(id+"F2.wireOp",EDGE,"E2.6.7.0")])],"isStart":false})}),makeQuery(id+"F3.boolean.opBoolean","COPY",FACE,{"derivedFrom":makeQuery(id+"F3.opExtrude","CAP_FACE",FACE,{"disambiguationData":[OSD([sQuery(id+"F2.wireOp",EDGE,"E2.6.8.0")])],"isStart":false})}),makeQuery(id+"F3.boolean.opBoolean","COPY",FACE,{"derivedFrom":makeQuery(id+"F3.opExtrude","CAP_FACE",FACE,{"disambiguationData":[OSD([sQuery(id+"F2.wireOp",EDGE,"E2.6.9.0")])],"isStart":false})}),makeQuery(id+"F3.boolean.opBoolean","COPY",FACE,{"derivedFrom":makeQuery(id+"F3.opExtrude","CAP_FACE",FACE,{"disambiguationData":[OSD([sQuery(id+"F2.wireOp",EDGE,"E2.6.10.0")])],"isStart":false})}),makeQuery(id+"F3.boolean.opBoolean","COPY",FACE,{"derivedFrom":makeQuery(id+"F3.opExtrude","CAP_FACE",FACE,{"disambiguationData":[OSD([sQuery(id+"F2.wireOp",EDGE,"E2.6.11.0")])],"isStart":false})}),makeQuery(id+"F3.boolean.opBoolean","COPY",FACE,{"derivedFrom":makeQuery(id+"F3.opExtrude","CAP_FACE",FACE,{"disambiguationData":[OSD([sQuery(id+"F2.wireOp",EDGE,"E2.7.0.0")])],"isStart":false})}),makeQuery(id+"F3.boolean.opBoolean","COPY",FACE,{"derivedFrom":makeQuery(id+"F3.opExtrude","CAP_FACE",FACE,{"disambiguationData":[OSD([sQuery(id+"F2.wireOp",EDGE,"E2.7.1.0")])],"isStart":false})}),makeQuery(id+"F3.boolean.opBoolean","COPY",FACE,{"derivedFrom":makeQuery(id+"F3.opExtrude","CAP_FACE",FACE,{"disambiguationData":[OSD([sQuery(id+"F2.wireOp",EDGE,"E2.7.2.0")])],"isStart":false})}),makeQuery(id+"F3.boolean.opBoolean","COPY",FACE,{"derivedFrom":makeQuery(id+"F3.opExtrude","CAP_FACE",FACE,{"disambiguationData":[OSD([sQuery(id+"F2.wireOp",EDGE,"E2.7.3.0")])],"isStart":false})}),makeQuery(id+"F3.boolean.opBoolean","COPY",FACE,{"derivedFrom":makeQuery(id+"F3.opExtrude","CAP_FACE",FACE,{"disambiguationData":[OSD([sQuery(id+"F2.wireOp",EDGE,"E2.7.4.0")])],"isStart":false})}),makeQuery(id+"F3.boolean.opBoolean","COPY",FACE,{"derivedFrom":makeQuery(id+"F3.opExtrude","CAP_FACE",FACE,{"disambiguationData":[OSD([sQuery(id+"F2.wireOp",EDGE,"E2.7.5.0")])],"isStart":false})}),makeQuery(id+"F3.boolean.opBoolean","COPY",FACE,{"derivedFrom":makeQuery(id+"F3.opExtrude","CAP_FACE",FACE,{"disambiguationData":[OSD([sQuery(id+"F2.wireOp",EDGE,"E2.7.6.0")])],"isStart":false})}),makeQuery(id+"F3.boolean.opBoolean","COPY",FACE,{"derivedFrom":makeQuery(id+"F3.opExtrude","CAP_FACE",FACE,{"disambiguationData":[OSD([sQuery(id+"F2.wireOp",EDGE,"E2.7.7.0")])],"isStart":false})}),makeQuery(id+"F3.boolean.opBoolean","COPY",FACE,{"derivedFrom":makeQuery(id+"F3.opExtrude","CAP_FACE",FACE,{"disambiguationData":[OSD([sQuery(id+"F2.wireOp",EDGE,"E2.7.8.0")])],"isStart":false})}),makeQuery(id+"F3.boolean.opBoolean","COPY",FACE,{"derivedFrom":makeQuery(id+"F3.opExtrude","CAP_FACE",FACE,{"disambiguationData":[OSD([sQuery(id+"F2.wireOp",EDGE,"E2.7.9.0")])],"isStart":false})}),makeQuery(id+"F3.boolean.opBoolean","COPY",FACE,{"derivedFrom":makeQuery(id+"F3.opExtrude","CAP_FACE",FACE,{"disambiguationData":[OSD([sQuery(id+"F2.wireOp",EDGE,"E2.7.10.0")])],"isStart":false})}),makeQuery(id+"F3.boolean.opBoolean","COPY",FACE,{"derivedFrom":makeQuery(id+"F3.opExtrude","CAP_FACE",FACE,{"disambiguationData":[OSD([sQuery(id+"F2.wireOp",EDGE,"E2.7.11.0")])],"isStart":false})}),makeQuery(id+"F3.boolean.opBoolean","COPY",FACE,{"derivedFrom":makeQuery(id+"F3.opExtrude","CAP_FACE",FACE,{"disambiguationData":[OSD([sQuery(id+"F2.wireOp",EDGE,"E2.8.0.0")])],"isStart":false})}),makeQuery(id+"F3.boolean.opBoolean","COPY",FACE,{"derivedFrom":makeQuery(id+"F3.opExtrude","CAP_FACE",FACE,{"disambiguationData":[OSD([sQuery(id+"F2.wireOp",EDGE,"E2.8.1.0")])],"isStart":false})}),makeQuery(id+"F3.boolean.opBoolean","COPY",FACE,{"derivedFrom":makeQuery(id+"F3.opExtrude","CAP_FACE",FACE,{"disambiguationData":[OSD([sQuery(id+"F2.wireOp",EDGE,"E2.8.2.0")])],"isStart":false})}),makeQuery(id+"F3.boolean.opBoolean","COPY",FACE,{"derivedFrom":makeQuery(id+"F3.opExtrude","CAP_FACE",FACE,{"disambiguationData":[OSD([sQuery(id+"F2.wireOp",EDGE,"E2.8.3.0")])],"isStart":false})}),makeQuery(id+"F3.boolean.opBoolean","COPY",FACE,{"derivedFrom":makeQuery(id+"F3.opExtrude","CAP_FACE",FACE,{"disambiguationData":[OSD([sQuery(id+"F2.wireOp",EDGE,"E2.8.4.0")])],"isStart":false})}),makeQuery(id+"F3.boolean.opBoolean","COPY",FACE,{"derivedFrom":makeQuery(id+"F3.opExtrude","CAP_FACE",FACE,{"disambiguationData":[OSD([sQuery(id+"F2.wireOp",EDGE,"E2.8.5.0")])],"isStart":false})}),makeQuery(id+"F3.boolean.opBoolean","COPY",FACE,{"derivedFrom":makeQuery(id+"F3.opExtrude","CAP_FACE",FACE,{"disambiguationData":[OSD([sQuery(id+"F2.wireOp",EDGE,"E2.8.6.0")])],"isStart":false})}),makeQuery(id+"F3.boolean.opBoolean","COPY",FACE,{"derivedFrom":makeQuery(id+"F3.opExtrude","CAP_FACE",FACE,{"disambiguationData":[OSD([sQuery(id+"F2.wireOp",EDGE,"E2.8.7.0")])],"isStart":false})}),makeQuery(id+"F3.boolean.opBoolean","COPY",FACE,{"derivedFrom":makeQuery(id+"F3.opExtrude","CAP_FACE",FACE,{"disambiguationData":[OSD([sQuery(id+"F2.wireOp",EDGE,"E2.8.8.0")])],"isStart":false})}),makeQuery(id+"F3.boolean.opBoolean","COPY",FACE,{"derivedFrom":makeQuery(id+"F3.opExtrude","CAP_FACE",FACE,{"disambiguationData":[OSD([sQuery(id+"F2.wireOp",EDGE,"E2.8.9.0")])],"isStart":false})}),makeQuery(id+"F3.boolean.opBoolean","COPY",FACE,{"derivedFrom":makeQuery(id+"F3.opExtrude","CAP_FACE",FACE,{"disambiguationData":[OSD([sQuery(id+"F2.wireOp",EDGE,"E2.8.10.0")])],"isStart":false})}),makeQuery(id+"F3.boolean.opBoolean","COPY",FACE,{"derivedFrom":makeQuery(id+"F3.opExtrude","CAP_FACE",FACE,{"disambiguationData":[OSD([sQuery(id+"F2.wireOp",EDGE,"E2.8.11.0")])],"isStart":false})}),makeQuery(id+"F3.boolean.opBoolean","COPY",FACE,{"derivedFrom":makeQuery(id+"F3.opExtrude","CAP_FACE",FACE,{"disambiguationData":[OSD([sQuery(id+"F2.wireOp",EDGE,"E2.9.0.0")])],"isStart":false})}),makeQuery(id+"F3.boolean.opBoolean","COPY",FACE,{"derivedFrom":makeQuery(id+"F3.opExtrude","CAP_FACE",FACE,{"disambiguationData":[OSD([sQuery(id+"F2.wireOp",EDGE,"E2.9.1.0")])],"isStart":false})}),makeQuery(id+"F3.boolean.opBoolean","COPY",FACE,{"derivedFrom":makeQuery(id+"F3.opExtrude","CAP_FACE",FACE,{"disambiguationData":[OSD([sQuery(id+"F2.wireOp",EDGE,"E2.9.2.0")])],"isStart":false})}),makeQuery(id+"F3.boolean.opBoolean","COPY",FACE,{"derivedFrom":makeQuery(id+"F3.opExtrude","CAP_FACE",FACE,{"disambiguationData":[OSD([sQuery(id+"F2.wireOp",EDGE,"E2.9.3.0")])],"isStart":false})}),makeQuery(id+"F3.boolean.opBoolean","COPY",FACE,{"derivedFrom":makeQuery(id+"F3.opExtrude","CAP_FACE",FACE,{"disambiguationData":[OSD([sQuery(id+"F2.wireOp",EDGE,"E2.9.4.0")])],"isStart":false})}),makeQuery(id+"F3.boolean.opBoolean","COPY",FACE,{"derivedFrom":makeQuery(id+"F3.opExtrude","CAP_FACE",FACE,{"disambiguationData":[OSD([sQuery(id+"F2.wireOp",EDGE,"E2.9.5.0")])],"isStart":false})}),makeQuery(id+"F3.boolean.opBoolean","COPY",FACE,{"derivedFrom":makeQuery(id+"F3.opExtrude","CAP_FACE",FACE,{"disambiguationData":[OSD([sQuery(id+"F2.wireOp",EDGE,"E2.9.6.0")])],"isStart":false})}),makeQuery(id+"F3.boolean.opBoolean","COPY",FACE,{"derivedFrom":makeQuery(id+"F3.opExtrude","CAP_FACE",FACE,{"disambiguationData":[OSD([sQuery(id+"F2.wireOp",EDGE,"E2.9.7.0")])],"isStart":false})}),makeQuery(id+"F3.boolean.opBoolean","COPY",FACE,{"derivedFrom":makeQuery(id+"F3.opExtrude","CAP_FACE",FACE,{"disambiguationData":[OSD([sQuery(id+"F2.wireOp",EDGE,"E2.9.8.0")])],"isStart":false})}),makeQuery(id+"F3.boolean.opBoolean","COPY",FACE,{"derivedFrom":makeQuery(id+"F3.opExtrude","CAP_FACE",FACE,{"disambiguationData":[OSD([sQuery(id+"F2.wireOp",EDGE,"E2.9.9.0")])],"isStart":false})}),makeQuery(id+"F3.boolean.opBoolean","COPY",FACE,{"derivedFrom":makeQuery(id+"F3.opExtrude","CAP_FACE",FACE,{"disambiguationData":[OSD([sQuery(id+"F2.wireOp",EDGE,"E2.9.10.0")])],"isStart":false})}),makeQuery(id+"F3.boolean.opBoolean","COPY",FACE,{"derivedFrom":makeQuery(id+"F3.opExtrude","CAP_FACE",FACE,{"disambiguationData":[OSD([sQuery(id+"F2.wireOp",EDGE,"E2.9.11.0")])],"isStart":false})}),makeQuery(id+"F3.boolean.opBoolean","COPY",FACE,{"derivedFrom":makeQuery(id+"F3.opExtrude","CAP_FACE",FACE,{"disambiguationData":[OSD([sQuery(id+"F2.wireOp",EDGE,"E2.10.0.0")])],"isStart":false})}),makeQuery(id+"F3.boolean.opBoolean","COPY",FACE,{"derivedFrom":makeQuery(id+"F3.opExtrude","CAP_FACE",FACE,{"disambiguationData":[OSD([sQuery(id+"F2.wireOp",EDGE,"E2.10.1.0")])],"isStart":false})}),makeQuery(id+"F3.boolean.opBoolean","COPY",FACE,{"derivedFrom":makeQuery(id+"F3.opExtrude","CAP_FACE",FACE,{"disambiguationData":[OSD([sQuery(id+"F2.wireOp",EDGE,"E2.10.2.0")])],"isStart":false})}),makeQuery(id+"F3.boolean.opBoolean","COPY",FACE,{"derivedFrom":makeQuery(id+"F3.opExtrude","CAP_FACE",FACE,{"disambiguationData":[OSD([sQuery(id+"F2.wireOp",EDGE,"E2.10.3.0")])],"isStart":false})}),makeQuery(id+"F3.boolean.opBoolean","COPY",FACE,{"derivedFrom":makeQuery(id+"F3.opExtrude","CAP_FACE",FACE,{"disambiguationData":[OSD([sQuery(id+"F2.wireOp",EDGE,"E2.10.4.0")])],"isStart":false})}),makeQuery(id+"F3.boolean.opBoolean","COPY",FACE,{"derivedFrom":makeQuery(id+"F3.opExtrude","CAP_FACE",FACE,{"disambiguationData":[OSD([sQuery(id+"F2.wireOp",EDGE,"E2.10.5.0")])],"isStart":false})}),makeQuery(id+"F3.boolean.opBoolean","COPY",FACE,{"derivedFrom":makeQuery(id+"F3.opExtrude","CAP_FACE",FACE,{"disambiguationData":[OSD([sQuery(id+"F2.wireOp",EDGE,"E2.10.6.0")])],"isStart":false})}),makeQuery(id+"F3.boolean.opBoolean","COPY",FACE,{"derivedFrom":makeQuery(id+"F3.opExtrude","CAP_FACE",FACE,{"disambiguationData":[OSD([sQuery(id+"F2.wireOp",EDGE,"E2.10.7.0")])],"isStart":false})}),makeQuery(id+"F3.boolean.opBoolean","COPY",FACE,{"derivedFrom":makeQuery(id+"F3.opExtrude","CAP_FACE",FACE,{"disambiguationData":[OSD([sQuery(id+"F2.wireOp",EDGE,"E2.10.8.0")])],"isStart":false})}),makeQuery(id+"F3.boolean.opBoolean","COPY",FACE,{"derivedFrom":makeQuery(id+"F3.opExtrude","CAP_FACE",FACE,{"disambiguationData":[OSD([sQuery(id+"F2.wireOp",EDGE,"E2.10.9.0")])],"isStart":false})}),makeQuery(id+"F3.boolean.opBoolean","COPY",FACE,{"derivedFrom":makeQuery(id+"F3.opExtrude","CAP_FACE",FACE,{"disambiguationData":[OSD([sQuery(id+"F2.wireOp",EDGE,"E2.10.10.0")])],"isStart":false})}),makeQuery(id+"F3.boolean.opBoolean","COPY",FACE,{"derivedFrom":makeQuery(id+"F3.opExtrude","CAP_FACE",FACE,{"disambiguationData":[OSD([sQuery(id+"F2.wireOp",EDGE,"E2.10.11.0")])],"isStart":false})}),makeQuery(id+"F3.boolean.opBoolean","COPY",FACE,{"derivedFrom":makeQuery(id+"F3.opExtrude","CAP_FACE",FACE,{"disambiguationData":[OSD([sQuery(id+"F2.wireOp",EDGE,"E2.11.0.0")])],"isStart":false})}),makeQuery(id+"F3.boolean.opBoolean","COPY",FACE,{"derivedFrom":makeQuery(id+"F3.opExtrude","CAP_FACE",FACE,{"disambiguationData":[OSD([sQuery(id+"F2.wireOp",EDGE,"E2.11.1.0")])],"isStart":false})}),makeQuery(id+"F3.boolean.opBoolean","COPY",FACE,{"derivedFrom":makeQuery(id+"F3.opExtrude","CAP_FACE",FACE,{"disambiguationData":[OSD([sQuery(id+"F2.wireOp",EDGE,"E2.11.2.0")])],"isStart":false})}),makeQuery(id+"F3.boolean.opBoolean","COPY",FACE,{"derivedFrom":makeQuery(id+"F3.opExtrude","CAP_FACE",FACE,{"disambiguationData":[OSD([sQuery(id+"F2.wireOp",EDGE,"E2.11.3.0")])],"isStart":false})}),makeQuery(id+"F3.boolean.opBoolean","COPY",FACE,{"derivedFrom":makeQuery(id+"F3.opExtrude","CAP_FACE",FACE,{"disambiguationData":[OSD([sQuery(id+"F2.wireOp",EDGE,"E2.11.4.0")])],"isStart":false})}),makeQuery(id+"F3.boolean.opBoolean","COPY",FACE,{"derivedFrom":makeQuery(id+"F3.opExtrude","CAP_FACE",FACE,{"disambiguationData":[OSD([sQuery(id+"F2.wireOp",EDGE,"E2.11.5.0")])],"isStart":false})}),makeQuery(id+"F3.boolean.opBoolean","COPY",FACE,{"derivedFrom":makeQuery(id+"F3.opExtrude","CAP_FACE",FACE,{"disambiguationData":[OSD([sQuery(id+"F2.wireOp",EDGE,"E2.11.6.0")])],"isStart":false})}),makeQuery(id+"F3.boolean.opBoolean","COPY",FACE,{"derivedFrom":makeQuery(id+"F3.opExtrude","CAP_FACE",FACE,{"disambiguationData":[OSD([sQuery(id+"F2.wireOp",EDGE,"E2.11.7.0")])],"isStart":false})}),makeQuery(id+"F3.boolean.opBoolean","COPY",FACE,{"derivedFrom":makeQuery(id+"F3.opExtrude","CAP_FACE",FACE,{"disambiguationData":[OSD([sQuery(id+"F2.wireOp",EDGE,"E2.11.8.0")])],"isStart":false})}),makeQuery(id+"F3.boolean.opBoolean","COPY",FACE,{"derivedFrom":makeQuery(id+"F3.opExtrude","CAP_FACE",FACE,{"disambiguationData":[OSD([sQuery(id+"F2.wireOp",EDGE,"E2.11.9.0")])],"isStart":false})}),makeQuery(id+"F3.boolean.opBoolean","COPY",FACE,{"derivedFrom":makeQuery(id+"F3.opExtrude","CAP_FACE",FACE,{"disambiguationData":[OSD([sQuery(id+"F2.wireOp",EDGE,"E2.11.10.0")])],"isStart":false})}),makeQuery(id+"F3.boolean.opBoolean","COPY",FACE,{"derivedFrom":makeQuery(id+"F3.opExtrude","CAP_FACE",FACE,{"disambiguationData":[OSD([sQuery(id+"F2.wireOp",EDGE,"E2.11.11.0")])],"isStart":false})}),makeQuery(id+"F3.boolean.opBoolean","COPY",FACE,{"derivedFrom":makeQuery(id+"F3.opExtrude","CAP_FACE",FACE,{"disambiguationData":[OSD([sQuery(id+"F2.wireOp",EDGE,"E2.12.0.0")])],"isStart":false})}),makeQuery(id+"F3.boolean.opBoolean","COPY",FACE,{"derivedFrom":makeQuery(id+"F3.opExtrude","CAP_FACE",FACE,{"disambiguationData":[OSD([sQuery(id+"F2.wireOp",EDGE,"E2.12.1.0")])],"isStart":false})}),makeQuery(id+"F3.boolean.opBoolean","COPY",FACE,{"derivedFrom":makeQuery(id+"F3.opExtrude","CAP_FACE",FACE,{"disambiguationData":[OSD([sQuery(id+"F2.wireOp",EDGE,"E2.12.2.0")])],"isStart":false})}),makeQuery(id+"F3.boolean.opBoolean","COPY",FACE,{"derivedFrom":makeQuery(id+"F3.opExtrude","CAP_FACE",FACE,{"disambiguationData":[OSD([sQuery(id+"F2.wireOp",EDGE,"E2.12.3.0")])],"isStart":false})}),makeQuery(id+"F3.boolean.opBoolean","COPY",FACE,{"derivedFrom":makeQuery(id+"F3.opExtrude","CAP_FACE",FACE,{"disambiguationData":[OSD([sQuery(id+"F2.wireOp",EDGE,"E2.12.4.0")])],"isStart":false})}),makeQuery(id+"F3.boolean.opBoolean","COPY",FACE,{"derivedFrom":makeQuery(id+"F3.opExtrude","CAP_FACE",FACE,{"disambiguationData":[OSD([sQuery(id+"F2.wireOp",EDGE,"E2.12.5.0")])],"isStart":false})}),makeQuery(id+"F3.boolean.opBoolean","COPY",FACE,{"derivedFrom":makeQuery(id+"F3.opExtrude","CAP_FACE",FACE,{"disambiguationData":[OSD([sQuery(id+"F2.wireOp",EDGE,"E2.12.6.0")])],"isStart":false})}),makeQuery(id+"F3.boolean.opBoolean","COPY",FACE,{"derivedFrom":makeQuery(id+"F3.opExtrude","CAP_FACE",FACE,{"disambiguationData":[OSD([sQuery(id+"F2.wireOp",EDGE,"E2.12.7.0")])],"isStart":false})}),makeQuery(id+"F3.boolean.opBoolean","COPY",FACE,{"derivedFrom":makeQuery(id+"F3.opExtrude","CAP_FACE",FACE,{"disambiguationData":[OSD([sQuery(id+"F2.wireOp",EDGE,"E2.12.8.0")])],"isStart":false})}),makeQuery(id+"F3.boolean.opBoolean","COPY",FACE,{"derivedFrom":makeQuery(id+"F3.opExtrude","CAP_FACE",FACE,{"disambiguationData":[OSD([sQuery(id+"F2.wireOp",EDGE,"E2.12.9.0")])],"isStart":false})}),makeQuery(id+"F3.boolean.opBoolean","COPY",FACE,{"derivedFrom":makeQuery(id+"F3.opExtrude","CAP_FACE",FACE,{"disambiguationData":[OSD([sQuery(id+"F2.wireOp",EDGE,"E2.12.10.0")])],"isStart":false})}),makeQuery(id+"F3.boolean.opBoolean","COPY",FACE,{"derivedFrom":makeQuery(id+"F3.opExtrude","CAP_FACE",FACE,{"disambiguationData":[OSD([sQuery(id+"F2.wireOp",EDGE,"E2.12.11.0")])],"isStart":false})}),makeQuery(id+"F3.boolean.opBoolean","COPY",FACE,{"derivedFrom":makeQuery(id+"F3.opExtrude","CAP_FACE",FACE,{"disambiguationData":[OSD([sQuery(id+"F2.wireOp",EDGE,"E2.13.0.0")])],"isStart":false})}),makeQuery(id+"F3.boolean.opBoolean","COPY",FACE,{"derivedFrom":makeQuery(id+"F3.opExtrude","CAP_FACE",FACE,{"disambiguationData":[OSD([sQuery(id+"F2.wireOp",EDGE,"E2.13.1.0")])],"isStart":false})}),makeQuery(id+"F3.boolean.opBoolean","COPY",FACE,{"derivedFrom":makeQuery(id+"F3.opExtrude","CAP_FACE",FACE,{"disambiguationData":[OSD([sQuery(id+"F2.wireOp",EDGE,"E2.13.2.0")])],"isStart":false})}),makeQuery(id+"F3.boolean.opBoolean","COPY",FACE,{"derivedFrom":makeQuery(id+"F3.opExtrude","CAP_FACE",FACE,{"disambiguationData":[OSD([sQuery(id+"F2.wireOp",EDGE,"E2.13.3.0")])],"isStart":false})}),makeQuery(id+"F3.boolean.opBoolean","COPY",FACE,{"derivedFrom":makeQuery(id+"F3.opExtrude","CAP_FACE",FACE,{"disambiguationData":[OSD([sQuery(id+"F2.wireOp",EDGE,"E2.13.4.0")])],"isStart":false})}),makeQuery(id+"F3.boolean.opBoolean","COPY",FACE,{"derivedFrom":makeQuery(id+"F3.opExtrude","CAP_FACE",FACE,{"disambiguationData":[OSD([sQuery(id+"F2.wireOp",EDGE,"E2.13.5.0")])],"isStart":false})}),makeQuery(id+"F3.boolean.opBoolean","COPY",FACE,{"derivedFrom":makeQuery(id+"F3.opExtrude","CAP_FACE",FACE,{"disambiguationData":[OSD([sQuery(id+"F2.wireOp",EDGE,"E2.13.6.0")])],"isStart":false})}),makeQuery(id+"F3.boolean.opBoolean","COPY",FACE,{"derivedFrom":makeQuery(id+"F3.opExtrude","CAP_FACE",FACE,{"disambiguationData":[OSD([sQuery(id+"F2.wireOp",EDGE,"E2.13.7.0")])],"isStart":false})}),makeQuery(id+"F3.boolean.opBoolean","COPY",FACE,{"derivedFrom":makeQuery(id+"F3.opExtrude","CAP_FACE",FACE,{"disambiguationData":[OSD([sQuery(id+"F2.wireOp",EDGE,"E2.13.8.0")])],"isStart":false})}),makeQuery(id+"F3.boolean.opBoolean","COPY",FACE,{"derivedFrom":makeQuery(id+"F3.opExtrude","CAP_FACE",FACE,{"disambiguationData":[OSD([sQuery(id+"F2.wireOp",EDGE,"E2.13.9.0")])],"isStart":false})}),makeQuery(id+"F3.boolean.opBoolean","COPY",FACE,{"derivedFrom":makeQuery(id+"F3.opExtrude","CAP_FACE",FACE,{"disambiguationData":[OSD([sQuery(id+"F2.wireOp",EDGE,"E2.13.10.0")])],"isStart":false})}),makeQuery(id+"F3.boolean.opBoolean","COPY",FACE,{"derivedFrom":makeQuery(id+"F3.opExtrude","CAP_FACE",FACE,{"disambiguationData":[OSD([sQuery(id+"F2.wireOp",EDGE,"E2.13.11.0")])],"isStart":false})}),makeQuery(id+"F3.boolean.opBoolean","COPY",FACE,{"derivedFrom":makeQuery(id+"F3.opExtrude","CAP_FACE",FACE,{"disambiguationData":[OSD([sQuery(id+"F2.wireOp",EDGE,"E2.14.0.0")])],"isStart":false})}),makeQuery(id+"F3.boolean.opBoolean","COPY",FACE,{"derivedFrom":makeQuery(id+"F3.opExtrude","CAP_FACE",FACE,{"disambiguationData":[OSD([sQuery(id+"F2.wireOp",EDGE,"E2.14.1.0")])],"isStart":false})}),makeQuery(id+"F3.boolean.opBoolean","COPY",FACE,{"derivedFrom":makeQuery(id+"F3.opExtrude","CAP_FACE",FACE,{"disambiguationData":[OSD([sQuery(id+"F2.wireOp",EDGE,"E2.14.2.0")])],"isStart":false})}),makeQuery(id+"F3.boolean.opBoolean","COPY",FACE,{"derivedFrom":makeQuery(id+"F3.opExtrude","CAP_FACE",FACE,{"disambiguationData":[OSD([sQuery(id+"F2.wireOp",EDGE,"E2.14.3.0")])],"isStart":false})}),makeQuery(id+"F3.boolean.opBoolean","COPY",FACE,{"derivedFrom":makeQuery(id+"F3.opExtrude","CAP_FACE",FACE,{"disambiguationData":[OSD([sQuery(id+"F2.wireOp",EDGE,"E2.14.4.0")])],"isStart":false})}),makeQuery(id+"F3.boolean.opBoolean","COPY",FACE,{"derivedFrom":makeQuery(id+"F3.opExtrude","CAP_FACE",FACE,{"disambiguationData":[OSD([sQuery(id+"F2.wireOp",EDGE,"E2.14.5.0")])],"isStart":false})}),makeQuery(id+"F3.boolean.opBoolean","COPY",FACE,{"derivedFrom":makeQuery(id+"F3.opExtrude","CAP_FACE",FACE,{"disambiguationData":[OSD([sQuery(id+"F2.wireOp",EDGE,"E2.14.6.0")])],"isStart":false})}),makeQuery(id+"F3.boolean.opBoolean","COPY",FACE,{"derivedFrom":makeQuery(id+"F3.opExtrude","CAP_FACE",FACE,{"disambiguationData":[OSD([sQuery(id+"F2.wireOp",EDGE,"E2.14.7.0")])],"isStart":false})}),makeQuery(id+"F3.boolean.opBoolean","COPY",FACE,{"derivedFrom":makeQuery(id+"F3.opExtrude","CAP_FACE",FACE,{"disambiguationData":[OSD([sQuery(id+"F2.wireOp",EDGE,"E2.14.8.0")])],"isStart":false})}),makeQuery(id+"F3.boolean.opBoolean","COPY",FACE,{"derivedFrom":makeQuery(id+"F3.opExtrude","CAP_FACE",FACE,{"disambiguationData":[OSD([sQuery(id+"F2.wireOp",EDGE,"E2.14.9.0")])],"isStart":false})}),makeQuery(id+"F3.boolean.opBoolean","COPY",FACE,{"derivedFrom":makeQuery(id+"F3.opExtrude","CAP_FACE",FACE,{"disambiguationData":[OSD([sQuery(id+"F2.wireOp",EDGE,"E2.14.10.0")])],"isStart":false})}),makeQuery(id+"F3.boolean.opBoolean","COPY",FACE,{"derivedFrom":makeQuery(id+"F3.opExtrude","CAP_FACE",FACE,{"disambiguationData":[OSD([sQuery(id+"F2.wireOp",EDGE,"E2.14.11.0")])],"isStart":false})}),makeQuery(id+"F3.boolean.opBoolean","COPY",FACE,{"derivedFrom":makeQuery(id+"F3.opExtrude","CAP_FACE",FACE,{"disambiguationData":[OSD([sQuery(id+"F2.wireOp",EDGE,"E2.15.0.0")])],"isStart":false})}),makeQuery(id+"F3.boolean.opBoolean","COPY",FACE,{"derivedFrom":makeQuery(id+"F3.opExtrude","CAP_FACE",FACE,{"disambiguationData":[OSD([sQuery(id+"F2.wireOp",EDGE,"E2.15.1.0")])],"isStart":false})}),makeQuery(id+"F3.boolean.opBoolean","COPY",FACE,{"derivedFrom":makeQuery(id+"F3.opExtrude","CAP_FACE",FACE,{"disambiguationData":[OSD([sQuery(id+"F2.wireOp",EDGE,"E2.15.2.0")])],"isStart":false})}),makeQuery(id+"F3.boolean.opBoolean","COPY",FACE,{"derivedFrom":makeQuery(id+"F3.opExtrude","CAP_FACE",FACE,{"disambiguationData":[OSD([sQuery(id+"F2.wireOp",EDGE,"E2.15.3.0")])],"isStart":false})}),makeQuery(id+"F3.boolean.opBoolean","COPY",FACE,{"derivedFrom":makeQuery(id+"F3.opExtrude","CAP_FACE",FACE,{"disambiguationData":[OSD([sQuery(id+"F2.wireOp",EDGE,"E2.15.4.0")])],"isStart":false})}),makeQuery(id+"F3.boolean.opBoolean","COPY",FACE,{"derivedFrom":makeQuery(id+"F3.opExtrude","CAP_FACE",FACE,{"disambiguationData":[OSD([sQuery(id+"F2.wireOp",EDGE,"E2.15.5.0")])],"isStart":false})}),makeQuery(id+"F3.boolean.opBoolean","COPY",FACE,{"derivedFrom":makeQuery(id+"F3.opExtrude","CAP_FACE",FACE,{"disambiguationData":[OSD([sQuery(id+"F2.wireOp",EDGE,"E2.15.6.0")])],"isStart":false})}),makeQuery(id+"F3.boolean.opBoolean","COPY",FACE,{"derivedFrom":makeQuery(id+"F3.opExtrude","CAP_FACE",FACE,{"disambiguationData":[OSD([sQuery(id+"F2.wireOp",EDGE,"E2.15.7.0")])],"isStart":false})}),makeQuery(id+"F3.boolean.opBoolean","COPY",FACE,{"derivedFrom":makeQuery(id+"F3.opExtrude","CAP_FACE",FACE,{"disambiguationData":[OSD([sQuery(id+"F2.wireOp",EDGE,"E2.15.8.0")])],"isStart":false})}),makeQuery(id+"F3.boolean.opBoolean","COPY",FACE,{"derivedFrom":makeQuery(id+"F3.opExtrude","CAP_FACE",FACE,{"disambiguationData":[OSD([sQuery(id+"F2.wireOp",EDGE,"E2.15.9.0")])],"isStart":false})}),makeQuery(id+"F3.boolean.opBoolean","COPY",FACE,{"derivedFrom":makeQuery(id+"F3.opExtrude","CAP_FACE",FACE,{"disambiguationData":[OSD([sQuery(id+"F2.wireOp",EDGE,"E2.15.10.0")])],"isStart":false})}),makeQuery(id+"F3.boolean.opBoolean","COPY",FACE,{"derivedFrom":makeQuery(id+"F3.opExtrude","CAP_FACE",FACE,{"disambiguationData":[OSD([sQuery(id+"F2.wireOp",EDGE,"E2.15.11.0")])],"isStart":false})}),makeQuery(id+"F3.boolean.opBoolean","COPY",FACE,{"derivedFrom":makeQuery(id+"F3.opExtrude","CAP_FACE",FACE,{"disambiguationData":[OSD([sQuery(id+"F2.wireOp",EDGE,"E2.16.0.0")])],"isStart":false})}),makeQuery(id+"F3.boolean.opBoolean","COPY",FACE,{"derivedFrom":makeQuery(id+"F3.opExtrude","CAP_FACE",FACE,{"disambiguationData":[OSD([sQuery(id+"F2.wireOp",EDGE,"E2.16.1.0")])],"isStart":false})}),makeQuery(id+"F3.boolean.opBoolean","COPY",FACE,{"derivedFrom":makeQuery(id+"F3.opExtrude","CAP_FACE",FACE,{"disambiguationData":[OSD([sQuery(id+"F2.wireOp",EDGE,"E2.16.2.0")])],"isStart":false})}),makeQuery(id+"F3.boolean.opBoolean","COPY",FACE,{"derivedFrom":makeQuery(id+"F3.opExtrude","CAP_FACE",FACE,{"disambiguationData":[OSD([sQuery(id+"F2.wireOp",EDGE,"E2.16.3.0")])],"isStart":false})}),makeQuery(id+"F3.boolean.opBoolean","COPY",FACE,{"derivedFrom":makeQuery(id+"F3.opExtrude","CAP_FACE",FACE,{"disambiguationData":[OSD([sQuery(id+"F2.wireOp",EDGE,"E2.16.4.0")])],"isStart":false})}),makeQuery(id+"F3.boolean.opBoolean","COPY",FACE,{"derivedFrom":makeQuery(id+"F3.opExtrude","CAP_FACE",FACE,{"disambiguationData":[OSD([sQuery(id+"F2.wireOp",EDGE,"E2.16.5.0")])],"isStart":false})}),makeQuery(id+"F3.boolean.opBoolean","COPY",FACE,{"derivedFrom":makeQuery(id+"F3.opExtrude","CAP_FACE",FACE,{"disambiguationData":[OSD([sQuery(id+"F2.wireOp",EDGE,"E2.16.6.0")])],"isStart":false})}),makeQuery(id+"F3.boolean.opBoolean","COPY",FACE,{"derivedFrom":makeQuery(id+"F3.opExtrude","CAP_FACE",FACE,{"disambiguationData":[OSD([sQuery(id+"F2.wireOp",EDGE,"E2.16.7.0")])],"isStart":false})}),makeQuery(id+"F3.boolean.opBoolean","COPY",FACE,{"derivedFrom":makeQuery(id+"F3.opExtrude","CAP_FACE",FACE,{"disambiguationData":[OSD([sQuery(id+"F2.wireOp",EDGE,"E2.16.8.0")])],"isStart":false})}),makeQuery(id+"F3.boolean.opBoolean","COPY",FACE,{"derivedFrom":makeQuery(id+"F3.opExtrude","CAP_FACE",FACE,{"disambiguationData":[OSD([sQuery(id+"F2.wireOp",EDGE,"E2.16.9.0")])],"isStart":false})}),makeQuery(id+"F3.boolean.opBoolean","COPY",FACE,{"derivedFrom":makeQuery(id+"F3.opExtrude","CAP_FACE",FACE,{"disambiguationData":[OSD([sQuery(id+"F2.wireOp",EDGE,"E2.16.10.0")])],"isStart":false})}),makeQuery(id+"F3.boolean.opBoolean","COPY",FACE,{"derivedFrom":makeQuery(id+"F3.opExtrude","CAP_FACE",FACE,{"disambiguationData":[OSD([sQuery(id+"F2.wireOp",EDGE,"E2.16.11.0")])],"isStart":false})}),makeQuery(id+"F3.boolean.opBoolean","COPY",FACE,{"derivedFrom":makeQuery(id+"F3.opExtrude","CAP_FACE",FACE,{"disambiguationData":[OSD([sQuery(id+"F2.wireOp",EDGE,"E2.17.0.0")])],"isStart":false})}),makeQuery(id+"F3.boolean.opBoolean","COPY",FACE,{"derivedFrom":makeQuery(id+"F3.opExtrude","CAP_FACE",FACE,{"disambiguationData":[OSD([sQuery(id+"F2.wireOp",EDGE,"E2.17.1.0")])],"isStart":false})}),makeQuery(id+"F3.boolean.opBoolean","COPY",FACE,{"derivedFrom":makeQuery(id+"F3.opExtrude","CAP_FACE",FACE,{"disambiguationData":[OSD([sQuery(id+"F2.wireOp",EDGE,"E2.17.2.0")])],"isStart":false})}),makeQuery(id+"F3.boolean.opBoolean","COPY",FACE,{"derivedFrom":makeQuery(id+"F3.opExtrude","CAP_FACE",FACE,{"disambiguationData":[OSD([sQuery(id+"F2.wireOp",EDGE,"E2.17.3.0")])],"isStart":false})}),makeQuery(id+"F3.boolean.opBoolean","COPY",FACE,{"derivedFrom":makeQuery(id+"F3.opExtrude","CAP_FACE",FACE,{"disambiguationData":[OSD([sQuery(id+"F2.wireOp",EDGE,"E2.17.4.0")])],"isStart":false})}),makeQuery(id+"F3.boolean.opBoolean","COPY",FACE,{"derivedFrom":makeQuery(id+"F3.opExtrude","CAP_FACE",FACE,{"disambiguationData":[OSD([sQuery(id+"F2.wireOp",EDGE,"E2.17.5.0")])],"isStart":false})}),makeQuery(id+"F3.boolean.opBoolean","COPY",FACE,{"derivedFrom":makeQuery(id+"F3.opExtrude","CAP_FACE",FACE,{"disambiguationData":[OSD([sQuery(id+"F2.wireOp",EDGE,"E2.17.6.0")])],"isStart":false})}),makeQuery(id+"F3.boolean.opBoolean","COPY",FACE,{"derivedFrom":makeQuery(id+"F3.opExtrude","CAP_FACE",FACE,{"disambiguationData":[OSD([sQuery(id+"F2.wireOp",EDGE,"E2.17.7.0")])],"isStart":false})}),makeQuery(id+"F3.boolean.opBoolean","COPY",FACE,{"derivedFrom":makeQuery(id+"F3.opExtrude","CAP_FACE",FACE,{"disambiguationData":[OSD([sQuery(id+"F2.wireOp",EDGE,"E2.17.8.0")])],"isStart":false})}),makeQuery(id+"F3.boolean.opBoolean","COPY",FACE,{"derivedFrom":makeQuery(id+"F3.opExtrude","CAP_FACE",FACE,{"disambiguationData":[OSD([sQuery(id+"F2.wireOp",EDGE,"E2.17.9.0")])],"isStart":false})}),makeQuery(id+"F3.boolean.opBoolean","COPY",FACE,{"derivedFrom":makeQuery(id+"F3.opExtrude","CAP_FACE",FACE,{"disambiguationData":[OSD([sQuery(id+"F2.wireOp",EDGE,"E2.17.10.0")])],"isStart":false})}),makeQuery(id+"F3.boolean.opBoolean","COPY",FACE,{"derivedFrom":makeQuery(id+"F3.opExtrude","CAP_FACE",FACE,{"disambiguationData":[OSD([sQuery(id+"F2.wireOp",EDGE,"E2.17.11.0")])],"isStart":false})}),makeQuery(id+"F3.boolean.opBoolean","COPY",FACE,{"derivedFrom":makeQuery(id+"F3.opExtrude","CAP_FACE",FACE,{"disambiguationData":[OSD([sQuery(id+"F2.wireOp",EDGE,"E2.18.0.0")])],"isStart":false})}),makeQuery(id+"F3.boolean.opBoolean","COPY",FACE,{"derivedFrom":makeQuery(id+"F3.opExtrude","CAP_FACE",FACE,{"disambiguationData":[OSD([sQuery(id+"F2.wireOp",EDGE,"E2.18.1.0")])],"isStart":false})}),makeQuery(id+"F3.boolean.opBoolean","COPY",FACE,{"derivedFrom":makeQuery(id+"F3.opExtrude","CAP_FACE",FACE,{"disambiguationData":[OSD([sQuery(id+"F2.wireOp",EDGE,"E2.18.2.0")])],"isStart":false})}),makeQuery(id+"F3.boolean.opBoolean","COPY",FACE,{"derivedFrom":makeQuery(id+"F3.opExtrude","CAP_FACE",FACE,{"disambiguationData":[OSD([sQuery(id+"F2.wireOp",EDGE,"E2.18.3.0")])],"isStart":false})}),makeQuery(id+"F3.boolean.opBoolean","COPY",FACE,{"derivedFrom":makeQuery(id+"F3.opExtrude","CAP_FACE",FACE,{"disambiguationData":[OSD([sQuery(id+"F2.wireOp",EDGE,"E2.18.4.0")])],"isStart":false})}),makeQuery(id+"F3.boolean.opBoolean","COPY",FACE,{"derivedFrom":makeQuery(id+"F3.opExtrude","CAP_FACE",FACE,{"disambiguationData":[OSD([sQuery(id+"F2.wireOp",EDGE,"E2.18.5.0")])],"isStart":false})}),makeQuery(id+"F3.boolean.opBoolean","COPY",FACE,{"derivedFrom":makeQuery(id+"F3.opExtrude","CAP_FACE",FACE,{"disambiguationData":[OSD([sQuery(id+"F2.wireOp",EDGE,"E2.18.6.0")])],"isStart":false})}),makeQuery(id+"F3.boolean.opBoolean","COPY",FACE,{"derivedFrom":makeQuery(id+"F3.opExtrude","CAP_FACE",FACE,{"disambiguationData":[OSD([sQuery(id+"F2.wireOp",EDGE,"E2.18.7.0")])],"isStart":false})}),makeQuery(id+"F3.boolean.opBoolean","COPY",FACE,{"derivedFrom":makeQuery(id+"F3.opExtrude","CAP_FACE",FACE,{"disambiguationData":[OSD([sQuery(id+"F2.wireOp",EDGE,"E2.18.8.0")])],"isStart":false})}),makeQuery(id+"F3.boolean.opBoolean","COPY",FACE,{"derivedFrom":makeQuery(id+"F3.opExtrude","CAP_FACE",FACE,{"disambiguationData":[OSD([sQuery(id+"F2.wireOp",EDGE,"E2.18.9.0")])],"isStart":false})}),makeQuery(id+"F3.boolean.opBoolean","COPY",FACE,{"derivedFrom":makeQuery(id+"F3.opExtrude","CAP_FACE",FACE,{"disambiguationData":[OSD([sQuery(id+"F2.wireOp",EDGE,"E2.18.10.0")])],"isStart":false})}),makeQuery(id+"F3.boolean.opBoolean","COPY",FACE,{"derivedFrom":makeQuery(id+"F3.opExtrude","CAP_FACE",FACE,{"disambiguationData":[OSD([sQuery(id+"F2.wireOp",EDGE,"E2.18.11.0")])],"isStart":false})}),makeQuery(id+"F8.opExtrude","CAP_FACE",FACE,{"disambiguationData":[OSD([sQuery(id+"F7.wireOp",EDGE,"E3.bottom"),sQuery(id+"F7.wireOp",EDGE,"E3.top"),sQuery(id+"F7.wireOp",EDGE,"E3.left"),sQuery(id+"F7.wireOp",EDGE,"E3.right")])],"isStart":false})]});
            var sketch = newSketch(context, id + "F9", { "sketchPlane" : qUnion([Q0])});
            skLineSegment(sketch, "E4.bottom", {"start": v(-17.78, 11.43) * mm, "end": v(17.78, 11.43) * mm});
            skLineSegment(sketch, "E4.top", {"start": v(-17.78, -11.43) * mm, "end": v(17.78, -11.43) * mm});
            skLineSegment(sketch, "E4.left", {"start": v(-17.78, 11.43) * mm, "end": v(-17.78, -11.43) * mm});
            skLineSegment(sketch, "E4.right", {"start": v(17.78, 11.43) * mm, "end": v(17.78, -11.43) * mm});
            skSolve(sketch);
        }
        {
            var Q0;
            Q0 = qSketchRegion(id + "F9", true);
            extrude(context, id + "F10", {"entities" : qUnion([Q0]), "operationType" : NewBodyOperationType.REMOVE, "oppositeDirection" : true, "depth" : 25.4 * mm, "offsetDistance" : 25.4 * mm});
        }
    });
